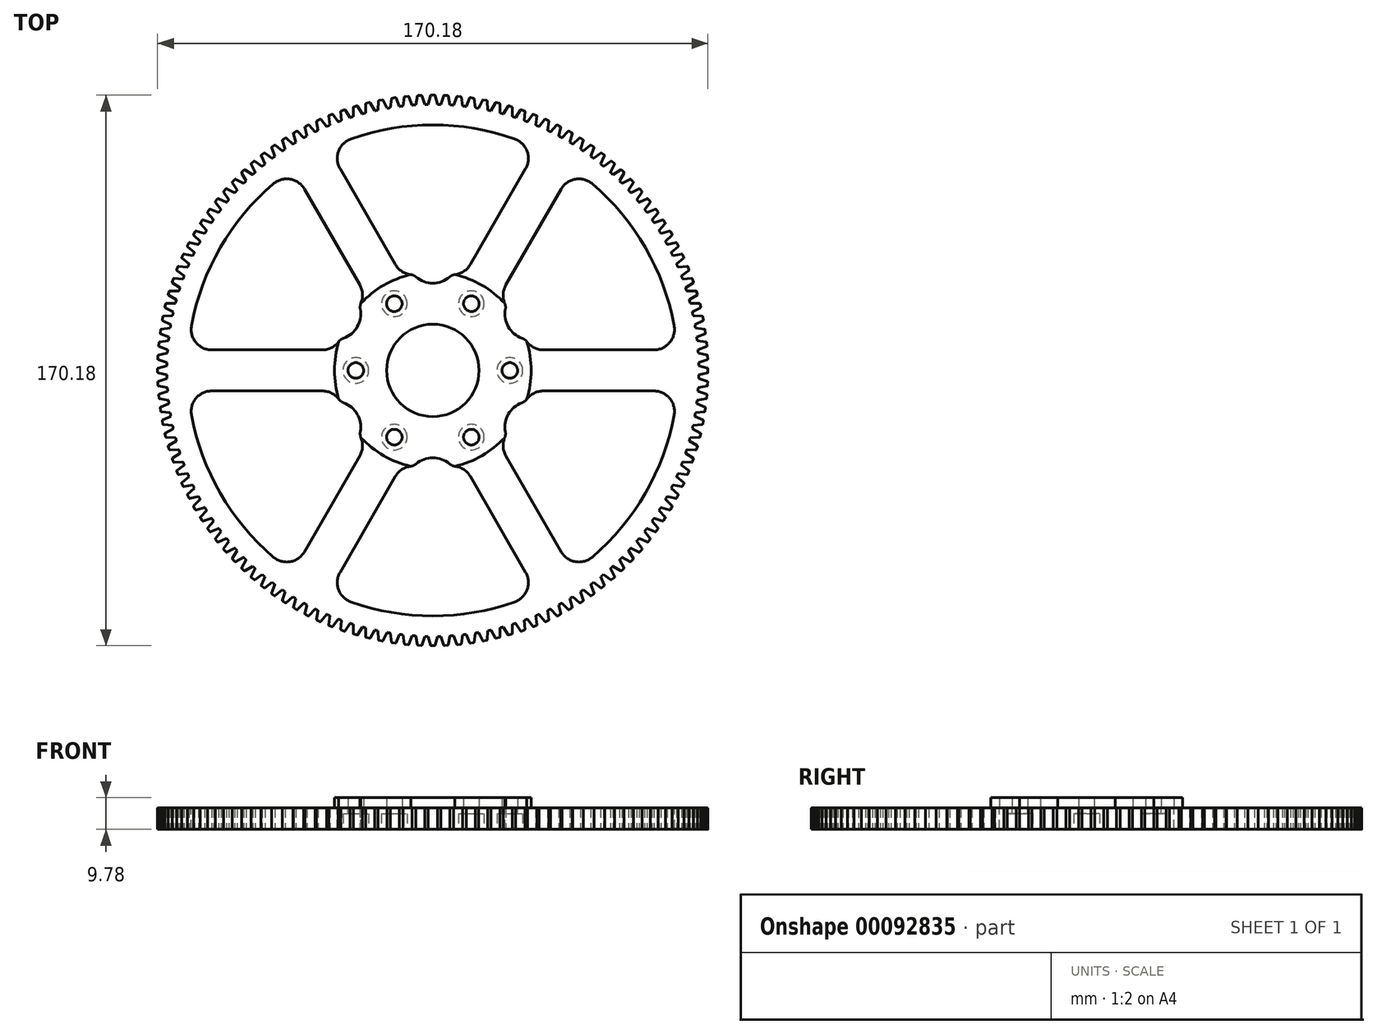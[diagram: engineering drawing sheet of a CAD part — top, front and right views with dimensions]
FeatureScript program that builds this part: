
annotation { "Feature Type Name" : "Feature", "Feature Type Description" : "" }
export const myFeature = defineFeature(function(context is Context, id is Id, definition is map)
    precondition{}
    {
        {
            var Q0;
            Q0=qCreatedBy(makeId("Top.planeOp"),FACE);
            var sketch = newSketch(context, id + "F0", { "sketchPlane" : qUnion([Q0])});
            skArc(sketch, "E0", {"start": v(-1.4, 82.23) * mm, "mid": v(-82.23, -1.4) * mm, "end": v(1.4, -82.23) * mm});
            skArc(sketch, "E1", {"start": v(1.4, -82.23) * mm, "mid": v(82.24, 0) * mm, "end": v(1.4, 82.23) * mm});
            skLineSegment(sketch, "E2", {"start": v(1.4, 82.23) * mm, "end": v(0.7, 84.97) * mm});
            skArc(sketch, "E3", {"start": v(0.7, 84.97) * mm, "mid": v(0.64, 85.06) * mm, "end": v(0.55, 85.1) * mm});
            skLineSegment(sketch, "E4", {"start": v(-1.4, 82.23) * mm, "end": v(-0.7, 84.97) * mm});
            skArc(sketch, "E5", {"start": v(-0.55, 85.1) * mm, "mid": v(-0.64, 85.06) * mm, "end": v(-0.7, 84.97) * mm});
            skLineSegment(sketch, "E6", {"start": v(-0.55, 85.1) * mm, "end": v(0.55, 85.1) * mm});
            skArc(sketch, "E7", {"start": v(1.4, 82.23) * mm, "mid": v(0, 82.24) * mm, "end": v(-1.4, 82.23) * mm});
            skSolve(sketch);
        }
        {
            var Q0;
            Q0=makeQuery(id+"F0.imprint","IMPRINT",FACE,{"disambiguationData":[TD([[makeQuery(id+"F0.imprint","IMPRINT",EDGE,{"derivedFrom":sQuery(id+"F0.wireOp",EDGE,"E0")}),1.0]])]});
            extrude(context, id + "F1", {"entities" : qUnion([Q0]), "depth" : 6.6 * mm, "symmetric" : true});
        }
        {
            var Q0;
            Q0=makeQuery(id+"F0.imprint","IMPRINT",FACE,{"disambiguationData":[TD([[makeQuery(id+"F0.imprint","IMPRINT",EDGE,{"derivedFrom":sQuery(id+"F0.wireOp",EDGE,"E2")}),1.0]])]});
            var Q1;
            Q1=makeQuery(id+"F1.opExtrude","CAP_FACE",FACE,{"disambiguationData":[OSD([sQuery(id+"F0.wireOp",EDGE,"E0"),sQuery(id+"F0.wireOp",EDGE,"E1"),sQuery(id+"F0.wireOp",EDGE,"E7")])],"isStart":false});
            var Q2;
            Q2=makeQuery(id+"F1.opExtrude","CAP_FACE",FACE,{"disambiguationData":[OSD([sQuery(id+"F0.wireOp",EDGE,"E0"),sQuery(id+"F0.wireOp",EDGE,"E1"),sQuery(id+"F0.wireOp",EDGE,"E7")])],"isStart":true});
            extrude(context, id + "F2", {"entities" : qUnion([Q0]), "endBound" : BoundingType.UP_TO_SURFACE, "endBoundEntityFace" : qUnion([Q1]), "depth" : 25.4 * mm, "hasSecondDirection" : true, "secondDirectionBound" : BoundingType.UP_TO_SURFACE, "secondDirectionOppositeDirection" : true, "secondDirectionBoundEntityFace" : qUnion([Q2]), "secondDirectionDepth" : 25.4 * mm});
        }
        {
            var Q0;
            Q0=makeQuery(id+"F2.opExtrude","SWEPT_BODY",BODY,{"disambiguationData":[OSD([sQuery(id+"F0.wireOp",EDGE,"E2"),sQuery(id+"F0.wireOp",EDGE,"E3"),sQuery(id+"F0.wireOp",EDGE,"E4"),sQuery(id+"F0.wireOp",EDGE,"E5"),sQuery(id+"F0.wireOp",EDGE,"E6"),sQuery(id+"F0.wireOp",EDGE,"E7")])]});
            var Q1;
            Q1=makeQuery(id+"F1.opExtrude","CAP_EDGE",EDGE,{"disambiguationData":[OSD([sQuery(id+"F0.wireOp",EDGE,"E0"),sQuery(id+"F0.wireOp",EDGE,"E1"),sQuery(id+"F0.wireOp",EDGE,"E7")])],"isStart":false});
            circularPattern(context, id + "F3", {"operationType" : NewBodyOperationType.ADD, "entities" : qUnion([Q0]), "axis" : qUnion([Q1]), "angle" : 360 * degree, "instanceCount" : 132, "oppositeDirection" : true, "equalSpace" : true});
        }
        {
            var Q0;
            {var subQ0=sQuery(id+"F0.wireOp",EDGE,"E7");var subQ1=makeQuery(id+"F2.opExtrude","CAP_FACE",FACE,{"disambiguationData":[OSD([sQuery(id+"F0.wireOp",EDGE,"E2"),sQuery(id+"F0.wireOp",EDGE,"E3"),sQuery(id+"F0.wireOp",EDGE,"E4"),sQuery(id+"F0.wireOp",EDGE,"E5"),sQuery(id+"F0.wireOp",EDGE,"E6"),subQ0])],"isStart":false});Q0=makeQuery(id+"F3.boolean.opBoolean","MERGE",FACE,{"derivedFrom":[makeQuery(id+"F1.opExtrude","CAP_FACE",FACE,{"disambiguationData":[OSD([sQuery(id+"F0.wireOp",EDGE,"E0"),sQuery(id+"F0.wireOp",EDGE,"E1"),subQ0])],"isStart":false}),subQ1,makeQuery(id+"F3.opPattern","COPY",FACE,{"derivedFrom":subQ1,"instanceName":"1"}),makeQuery(id+"F3.opPattern","COPY",FACE,{"derivedFrom":subQ1,"instanceName":"2"}),makeQuery(id+"F3.opPattern","COPY",FACE,{"derivedFrom":subQ1,"instanceName":"3"}),makeQuery(id+"F3.opPattern","COPY",FACE,{"derivedFrom":subQ1,"instanceName":"4"}),makeQuery(id+"F3.opPattern","COPY",FACE,{"derivedFrom":subQ1,"instanceName":"5"}),makeQuery(id+"F3.opPattern","COPY",FACE,{"derivedFrom":subQ1,"instanceName":"6"}),makeQuery(id+"F3.opPattern","COPY",FACE,{"derivedFrom":subQ1,"instanceName":"7"}),makeQuery(id+"F3.opPattern","COPY",FACE,{"derivedFrom":subQ1,"instanceName":"8"}),makeQuery(id+"F3.opPattern","COPY",FACE,{"derivedFrom":subQ1,"instanceName":"9"}),makeQuery(id+"F3.opPattern","COPY",FACE,{"derivedFrom":subQ1,"instanceName":"10"}),makeQuery(id+"F3.opPattern","COPY",FACE,{"derivedFrom":subQ1,"instanceName":"11"}),makeQuery(id+"F3.opPattern","COPY",FACE,{"derivedFrom":subQ1,"instanceName":"12"}),makeQuery(id+"F3.opPattern","COPY",FACE,{"derivedFrom":subQ1,"instanceName":"13"}),makeQuery(id+"F3.opPattern","COPY",FACE,{"derivedFrom":subQ1,"instanceName":"14"}),makeQuery(id+"F3.opPattern","COPY",FACE,{"derivedFrom":subQ1,"instanceName":"15"}),makeQuery(id+"F3.opPattern","COPY",FACE,{"derivedFrom":subQ1,"instanceName":"16"}),makeQuery(id+"F3.opPattern","COPY",FACE,{"derivedFrom":subQ1,"instanceName":"17"}),makeQuery(id+"F3.opPattern","COPY",FACE,{"derivedFrom":subQ1,"instanceName":"18"}),makeQuery(id+"F3.opPattern","COPY",FACE,{"derivedFrom":subQ1,"instanceName":"19"}),makeQuery(id+"F3.opPattern","COPY",FACE,{"derivedFrom":subQ1,"instanceName":"20"}),makeQuery(id+"F3.opPattern","COPY",FACE,{"derivedFrom":subQ1,"instanceName":"21"}),makeQuery(id+"F3.opPattern","COPY",FACE,{"derivedFrom":subQ1,"instanceName":"22"}),makeQuery(id+"F3.opPattern","COPY",FACE,{"derivedFrom":subQ1,"instanceName":"23"}),makeQuery(id+"F3.opPattern","COPY",FACE,{"derivedFrom":subQ1,"instanceName":"24"}),makeQuery(id+"F3.opPattern","COPY",FACE,{"derivedFrom":subQ1,"instanceName":"25"}),makeQuery(id+"F3.opPattern","COPY",FACE,{"derivedFrom":subQ1,"instanceName":"26"}),makeQuery(id+"F3.opPattern","COPY",FACE,{"derivedFrom":subQ1,"instanceName":"27"}),makeQuery(id+"F3.opPattern","COPY",FACE,{"derivedFrom":subQ1,"instanceName":"28"}),makeQuery(id+"F3.opPattern","COPY",FACE,{"derivedFrom":subQ1,"instanceName":"29"}),makeQuery(id+"F3.opPattern","COPY",FACE,{"derivedFrom":subQ1,"instanceName":"30"}),makeQuery(id+"F3.opPattern","COPY",FACE,{"derivedFrom":subQ1,"instanceName":"31"}),makeQuery(id+"F3.opPattern","COPY",FACE,{"derivedFrom":subQ1,"instanceName":"32"}),makeQuery(id+"F3.opPattern","COPY",FACE,{"derivedFrom":subQ1,"instanceName":"33"}),makeQuery(id+"F3.opPattern","COPY",FACE,{"derivedFrom":subQ1,"instanceName":"34"}),makeQuery(id+"F3.opPattern","COPY",FACE,{"derivedFrom":subQ1,"instanceName":"35"}),makeQuery(id+"F3.opPattern","COPY",FACE,{"derivedFrom":subQ1,"instanceName":"36"}),makeQuery(id+"F3.opPattern","COPY",FACE,{"derivedFrom":subQ1,"instanceName":"37"}),makeQuery(id+"F3.opPattern","COPY",FACE,{"derivedFrom":subQ1,"instanceName":"38"}),makeQuery(id+"F3.opPattern","COPY",FACE,{"derivedFrom":subQ1,"instanceName":"39"}),makeQuery(id+"F3.opPattern","COPY",FACE,{"derivedFrom":subQ1,"instanceName":"40"}),makeQuery(id+"F3.opPattern","COPY",FACE,{"derivedFrom":subQ1,"instanceName":"41"}),makeQuery(id+"F3.opPattern","COPY",FACE,{"derivedFrom":subQ1,"instanceName":"42"}),makeQuery(id+"F3.opPattern","COPY",FACE,{"derivedFrom":subQ1,"instanceName":"43"}),makeQuery(id+"F3.opPattern","COPY",FACE,{"derivedFrom":subQ1,"instanceName":"44"}),makeQuery(id+"F3.opPattern","COPY",FACE,{"derivedFrom":subQ1,"instanceName":"45"}),makeQuery(id+"F3.opPattern","COPY",FACE,{"derivedFrom":subQ1,"instanceName":"46"}),makeQuery(id+"F3.opPattern","COPY",FACE,{"derivedFrom":subQ1,"instanceName":"47"}),makeQuery(id+"F3.opPattern","COPY",FACE,{"derivedFrom":subQ1,"instanceName":"48"}),makeQuery(id+"F3.opPattern","COPY",FACE,{"derivedFrom":subQ1,"instanceName":"49"}),makeQuery(id+"F3.opPattern","COPY",FACE,{"derivedFrom":subQ1,"instanceName":"50"}),makeQuery(id+"F3.opPattern","COPY",FACE,{"derivedFrom":subQ1,"instanceName":"51"}),makeQuery(id+"F3.opPattern","COPY",FACE,{"derivedFrom":subQ1,"instanceName":"52"}),makeQuery(id+"F3.opPattern","COPY",FACE,{"derivedFrom":subQ1,"instanceName":"53"}),makeQuery(id+"F3.opPattern","COPY",FACE,{"derivedFrom":subQ1,"instanceName":"54"}),makeQuery(id+"F3.opPattern","COPY",FACE,{"derivedFrom":subQ1,"instanceName":"55"}),makeQuery(id+"F3.opPattern","COPY",FACE,{"derivedFrom":subQ1,"instanceName":"56"}),makeQuery(id+"F3.opPattern","COPY",FACE,{"derivedFrom":subQ1,"instanceName":"57"}),makeQuery(id+"F3.opPattern","COPY",FACE,{"derivedFrom":subQ1,"instanceName":"58"}),makeQuery(id+"F3.opPattern","COPY",FACE,{"derivedFrom":subQ1,"instanceName":"59"}),makeQuery(id+"F3.opPattern","COPY",FACE,{"derivedFrom":subQ1,"instanceName":"60"}),makeQuery(id+"F3.opPattern","COPY",FACE,{"derivedFrom":subQ1,"instanceName":"61"}),makeQuery(id+"F3.opPattern","COPY",FACE,{"derivedFrom":subQ1,"instanceName":"62"}),makeQuery(id+"F3.opPattern","COPY",FACE,{"derivedFrom":subQ1,"instanceName":"63"}),makeQuery(id+"F3.opPattern","COPY",FACE,{"derivedFrom":subQ1,"instanceName":"64"}),makeQuery(id+"F3.opPattern","COPY",FACE,{"derivedFrom":subQ1,"instanceName":"65"}),makeQuery(id+"F3.opPattern","COPY",FACE,{"derivedFrom":subQ1,"instanceName":"66"}),makeQuery(id+"F3.opPattern","COPY",FACE,{"derivedFrom":subQ1,"instanceName":"67"}),makeQuery(id+"F3.opPattern","COPY",FACE,{"derivedFrom":subQ1,"instanceName":"68"}),makeQuery(id+"F3.opPattern","COPY",FACE,{"derivedFrom":subQ1,"instanceName":"69"}),makeQuery(id+"F3.opPattern","COPY",FACE,{"derivedFrom":subQ1,"instanceName":"70"}),makeQuery(id+"F3.opPattern","COPY",FACE,{"derivedFrom":subQ1,"instanceName":"71"}),makeQuery(id+"F3.opPattern","COPY",FACE,{"derivedFrom":subQ1,"instanceName":"72"}),makeQuery(id+"F3.opPattern","COPY",FACE,{"derivedFrom":subQ1,"instanceName":"73"}),makeQuery(id+"F3.opPattern","COPY",FACE,{"derivedFrom":subQ1,"instanceName":"74"}),makeQuery(id+"F3.opPattern","COPY",FACE,{"derivedFrom":subQ1,"instanceName":"75"}),makeQuery(id+"F3.opPattern","COPY",FACE,{"derivedFrom":subQ1,"instanceName":"76"}),makeQuery(id+"F3.opPattern","COPY",FACE,{"derivedFrom":subQ1,"instanceName":"77"}),makeQuery(id+"F3.opPattern","COPY",FACE,{"derivedFrom":subQ1,"instanceName":"78"}),makeQuery(id+"F3.opPattern","COPY",FACE,{"derivedFrom":subQ1,"instanceName":"79"}),makeQuery(id+"F3.opPattern","COPY",FACE,{"derivedFrom":subQ1,"instanceName":"80"}),makeQuery(id+"F3.opPattern","COPY",FACE,{"derivedFrom":subQ1,"instanceName":"81"}),makeQuery(id+"F3.opPattern","COPY",FACE,{"derivedFrom":subQ1,"instanceName":"82"}),makeQuery(id+"F3.opPattern","COPY",FACE,{"derivedFrom":subQ1,"instanceName":"83"}),makeQuery(id+"F3.opPattern","COPY",FACE,{"derivedFrom":subQ1,"instanceName":"84"}),makeQuery(id+"F3.opPattern","COPY",FACE,{"derivedFrom":subQ1,"instanceName":"85"}),makeQuery(id+"F3.opPattern","COPY",FACE,{"derivedFrom":subQ1,"instanceName":"86"}),makeQuery(id+"F3.opPattern","COPY",FACE,{"derivedFrom":subQ1,"instanceName":"87"}),makeQuery(id+"F3.opPattern","COPY",FACE,{"derivedFrom":subQ1,"instanceName":"88"}),makeQuery(id+"F3.opPattern","COPY",FACE,{"derivedFrom":subQ1,"instanceName":"89"}),makeQuery(id+"F3.opPattern","COPY",FACE,{"derivedFrom":subQ1,"instanceName":"90"}),makeQuery(id+"F3.opPattern","COPY",FACE,{"derivedFrom":subQ1,"instanceName":"91"}),makeQuery(id+"F3.opPattern","COPY",FACE,{"derivedFrom":subQ1,"instanceName":"92"}),makeQuery(id+"F3.opPattern","COPY",FACE,{"derivedFrom":subQ1,"instanceName":"93"}),makeQuery(id+"F3.opPattern","COPY",FACE,{"derivedFrom":subQ1,"instanceName":"94"}),makeQuery(id+"F3.opPattern","COPY",FACE,{"derivedFrom":subQ1,"instanceName":"95"}),makeQuery(id+"F3.opPattern","COPY",FACE,{"derivedFrom":subQ1,"instanceName":"96"}),makeQuery(id+"F3.opPattern","COPY",FACE,{"derivedFrom":subQ1,"instanceName":"97"}),makeQuery(id+"F3.opPattern","COPY",FACE,{"derivedFrom":subQ1,"instanceName":"98"}),makeQuery(id+"F3.opPattern","COPY",FACE,{"derivedFrom":subQ1,"instanceName":"99"}),makeQuery(id+"F3.opPattern","COPY",FACE,{"derivedFrom":subQ1,"instanceName":"100"}),makeQuery(id+"F3.opPattern","COPY",FACE,{"derivedFrom":subQ1,"instanceName":"101"}),makeQuery(id+"F3.opPattern","COPY",FACE,{"derivedFrom":subQ1,"instanceName":"102"}),makeQuery(id+"F3.opPattern","COPY",FACE,{"derivedFrom":subQ1,"instanceName":"103"}),makeQuery(id+"F3.opPattern","COPY",FACE,{"derivedFrom":subQ1,"instanceName":"104"}),makeQuery(id+"F3.opPattern","COPY",FACE,{"derivedFrom":subQ1,"instanceName":"105"}),makeQuery(id+"F3.opPattern","COPY",FACE,{"derivedFrom":subQ1,"instanceName":"106"}),makeQuery(id+"F3.opPattern","COPY",FACE,{"derivedFrom":subQ1,"instanceName":"107"}),makeQuery(id+"F3.opPattern","COPY",FACE,{"derivedFrom":subQ1,"instanceName":"108"}),makeQuery(id+"F3.opPattern","COPY",FACE,{"derivedFrom":subQ1,"instanceName":"109"}),makeQuery(id+"F3.opPattern","COPY",FACE,{"derivedFrom":subQ1,"instanceName":"110"}),makeQuery(id+"F3.opPattern","COPY",FACE,{"derivedFrom":subQ1,"instanceName":"111"}),makeQuery(id+"F3.opPattern","COPY",FACE,{"derivedFrom":subQ1,"instanceName":"112"}),makeQuery(id+"F3.opPattern","COPY",FACE,{"derivedFrom":subQ1,"instanceName":"113"}),makeQuery(id+"F3.opPattern","COPY",FACE,{"derivedFrom":subQ1,"instanceName":"114"}),makeQuery(id+"F3.opPattern","COPY",FACE,{"derivedFrom":subQ1,"instanceName":"115"}),makeQuery(id+"F3.opPattern","COPY",FACE,{"derivedFrom":subQ1,"instanceName":"116"}),makeQuery(id+"F3.opPattern","COPY",FACE,{"derivedFrom":subQ1,"instanceName":"117"}),makeQuery(id+"F3.opPattern","COPY",FACE,{"derivedFrom":subQ1,"instanceName":"118"}),makeQuery(id+"F3.opPattern","COPY",FACE,{"derivedFrom":subQ1,"instanceName":"119"}),makeQuery(id+"F3.opPattern","COPY",FACE,{"derivedFrom":subQ1,"instanceName":"120"}),makeQuery(id+"F3.opPattern","COPY",FACE,{"derivedFrom":subQ1,"instanceName":"121"}),makeQuery(id+"F3.opPattern","COPY",FACE,{"derivedFrom":subQ1,"instanceName":"122"}),makeQuery(id+"F3.opPattern","COPY",FACE,{"derivedFrom":subQ1,"instanceName":"123"}),makeQuery(id+"F3.opPattern","COPY",FACE,{"derivedFrom":subQ1,"instanceName":"124"}),makeQuery(id+"F3.opPattern","COPY",FACE,{"derivedFrom":subQ1,"instanceName":"125"}),makeQuery(id+"F3.opPattern","COPY",FACE,{"derivedFrom":subQ1,"instanceName":"126"}),makeQuery(id+"F3.opPattern","COPY",FACE,{"derivedFrom":subQ1,"instanceName":"127"}),makeQuery(id+"F3.opPattern","COPY",FACE,{"derivedFrom":subQ1,"instanceName":"128"}),makeQuery(id+"F3.opPattern","COPY",FACE,{"derivedFrom":subQ1,"instanceName":"129"}),makeQuery(id+"F3.opPattern","COPY",FACE,{"derivedFrom":subQ1,"instanceName":"130"}),makeQuery(id+"F3.opPattern","COPY",FACE,{"derivedFrom":subQ1,"instanceName":"131"})]});}
            var sketch = newSketch(context, id + "F4", { "sketchPlane" : qUnion([Q0])});
            skCircle(sketch, "E8", {"center": v(0, 0) * mm, "radius": 14.29 * mm});
            skCircle(sketch, "E9.cCircle", {"center": v(0, 0) * mm, "radius": 23.81 * mm, "construction": true});
            skLineSegment(sketch, "E9.0", {"start": v(23.81, 0) * mm, "end": v(11.9, -20.62) * mm, "construction": true});
            skLineSegment(sketch, "E9.1", {"start": v(11.9, -20.62) * mm, "end": v(-11.9, -20.62) * mm, "construction": true});
            skLineSegment(sketch, "E9.2", {"start": v(-11.9, -20.62) * mm, "end": v(-23.81, 0) * mm, "construction": true});
            skLineSegment(sketch, "E9.3", {"start": v(-23.81, 0) * mm, "end": v(-11.9, 20.62) * mm, "construction": true});
            skLineSegment(sketch, "E9.4", {"start": v(-11.9, 20.62) * mm, "end": v(11.9, 20.62) * mm, "construction": true});
            skLineSegment(sketch, "E9.5", {"start": v(11.9, 20.62) * mm, "end": v(23.81, 0) * mm, "construction": true});
            skCircle(sketch, "E10", {"center": v(-11.9, 20.62) * mm, "radius": 2.41 * mm});
            skCircle(sketch, "E11", {"center": v(-23.81, 0) * mm, "radius": 2.41 * mm});
            skCircle(sketch, "E12", {"center": v(-11.9, -20.62) * mm, "radius": 2.41 * mm});
            skCircle(sketch, "E13", {"center": v(11.9, -20.62) * mm, "radius": 2.41 * mm});
            skCircle(sketch, "E14", {"center": v(23.81, 0) * mm, "radius": 2.41 * mm});
            skCircle(sketch, "E15", {"center": v(11.9, 20.62) * mm, "radius": 2.41 * mm});
            skSolve(sketch);
        }
        {
            var Q0;
            Q0=qSketchRegion(id+"F4",true);
            extrude(context, id + "F5", {"entities" : qUnion([Q0]), "operationType" : NewBodyOperationType.REMOVE, "endBound" : BoundingType.THROUGH_ALL, "oppositeDirection" : true, "depth" : 25.4 * mm});
        }
        {
            var Q0;
            {var subQ0=sQuery(id+"F0.wireOp",EDGE,"E7");var subQ1=makeQuery(id+"F2.opExtrude","CAP_FACE",FACE,{"disambiguationData":[OSD([sQuery(id+"F0.wireOp",EDGE,"E2"),sQuery(id+"F0.wireOp",EDGE,"E3"),sQuery(id+"F0.wireOp",EDGE,"E4"),sQuery(id+"F0.wireOp",EDGE,"E5"),sQuery(id+"F0.wireOp",EDGE,"E6"),subQ0])],"isStart":false});Q0=makeQuery(id+"F3.boolean.opBoolean","MERGE",FACE,{"derivedFrom":[makeQuery(id+"F1.opExtrude","CAP_FACE",FACE,{"disambiguationData":[OSD([sQuery(id+"F0.wireOp",EDGE,"E0"),sQuery(id+"F0.wireOp",EDGE,"E1"),subQ0])],"isStart":false}),subQ1,makeQuery(id+"F3.opPattern","COPY",FACE,{"derivedFrom":subQ1,"instanceName":"1"}),makeQuery(id+"F3.opPattern","COPY",FACE,{"derivedFrom":subQ1,"instanceName":"2"}),makeQuery(id+"F3.opPattern","COPY",FACE,{"derivedFrom":subQ1,"instanceName":"3"}),makeQuery(id+"F3.opPattern","COPY",FACE,{"derivedFrom":subQ1,"instanceName":"4"}),makeQuery(id+"F3.opPattern","COPY",FACE,{"derivedFrom":subQ1,"instanceName":"5"}),makeQuery(id+"F3.opPattern","COPY",FACE,{"derivedFrom":subQ1,"instanceName":"6"}),makeQuery(id+"F3.opPattern","COPY",FACE,{"derivedFrom":subQ1,"instanceName":"7"}),makeQuery(id+"F3.opPattern","COPY",FACE,{"derivedFrom":subQ1,"instanceName":"8"}),makeQuery(id+"F3.opPattern","COPY",FACE,{"derivedFrom":subQ1,"instanceName":"9"}),makeQuery(id+"F3.opPattern","COPY",FACE,{"derivedFrom":subQ1,"instanceName":"10"}),makeQuery(id+"F3.opPattern","COPY",FACE,{"derivedFrom":subQ1,"instanceName":"11"}),makeQuery(id+"F3.opPattern","COPY",FACE,{"derivedFrom":subQ1,"instanceName":"12"}),makeQuery(id+"F3.opPattern","COPY",FACE,{"derivedFrom":subQ1,"instanceName":"13"}),makeQuery(id+"F3.opPattern","COPY",FACE,{"derivedFrom":subQ1,"instanceName":"14"}),makeQuery(id+"F3.opPattern","COPY",FACE,{"derivedFrom":subQ1,"instanceName":"15"}),makeQuery(id+"F3.opPattern","COPY",FACE,{"derivedFrom":subQ1,"instanceName":"16"}),makeQuery(id+"F3.opPattern","COPY",FACE,{"derivedFrom":subQ1,"instanceName":"17"}),makeQuery(id+"F3.opPattern","COPY",FACE,{"derivedFrom":subQ1,"instanceName":"18"}),makeQuery(id+"F3.opPattern","COPY",FACE,{"derivedFrom":subQ1,"instanceName":"19"}),makeQuery(id+"F3.opPattern","COPY",FACE,{"derivedFrom":subQ1,"instanceName":"20"}),makeQuery(id+"F3.opPattern","COPY",FACE,{"derivedFrom":subQ1,"instanceName":"21"}),makeQuery(id+"F3.opPattern","COPY",FACE,{"derivedFrom":subQ1,"instanceName":"22"}),makeQuery(id+"F3.opPattern","COPY",FACE,{"derivedFrom":subQ1,"instanceName":"23"}),makeQuery(id+"F3.opPattern","COPY",FACE,{"derivedFrom":subQ1,"instanceName":"24"}),makeQuery(id+"F3.opPattern","COPY",FACE,{"derivedFrom":subQ1,"instanceName":"25"}),makeQuery(id+"F3.opPattern","COPY",FACE,{"derivedFrom":subQ1,"instanceName":"26"}),makeQuery(id+"F3.opPattern","COPY",FACE,{"derivedFrom":subQ1,"instanceName":"27"}),makeQuery(id+"F3.opPattern","COPY",FACE,{"derivedFrom":subQ1,"instanceName":"28"}),makeQuery(id+"F3.opPattern","COPY",FACE,{"derivedFrom":subQ1,"instanceName":"29"}),makeQuery(id+"F3.opPattern","COPY",FACE,{"derivedFrom":subQ1,"instanceName":"30"}),makeQuery(id+"F3.opPattern","COPY",FACE,{"derivedFrom":subQ1,"instanceName":"31"}),makeQuery(id+"F3.opPattern","COPY",FACE,{"derivedFrom":subQ1,"instanceName":"32"}),makeQuery(id+"F3.opPattern","COPY",FACE,{"derivedFrom":subQ1,"instanceName":"33"}),makeQuery(id+"F3.opPattern","COPY",FACE,{"derivedFrom":subQ1,"instanceName":"34"}),makeQuery(id+"F3.opPattern","COPY",FACE,{"derivedFrom":subQ1,"instanceName":"35"}),makeQuery(id+"F3.opPattern","COPY",FACE,{"derivedFrom":subQ1,"instanceName":"36"}),makeQuery(id+"F3.opPattern","COPY",FACE,{"derivedFrom":subQ1,"instanceName":"37"}),makeQuery(id+"F3.opPattern","COPY",FACE,{"derivedFrom":subQ1,"instanceName":"38"}),makeQuery(id+"F3.opPattern","COPY",FACE,{"derivedFrom":subQ1,"instanceName":"39"}),makeQuery(id+"F3.opPattern","COPY",FACE,{"derivedFrom":subQ1,"instanceName":"40"}),makeQuery(id+"F3.opPattern","COPY",FACE,{"derivedFrom":subQ1,"instanceName":"41"}),makeQuery(id+"F3.opPattern","COPY",FACE,{"derivedFrom":subQ1,"instanceName":"42"}),makeQuery(id+"F3.opPattern","COPY",FACE,{"derivedFrom":subQ1,"instanceName":"43"}),makeQuery(id+"F3.opPattern","COPY",FACE,{"derivedFrom":subQ1,"instanceName":"44"}),makeQuery(id+"F3.opPattern","COPY",FACE,{"derivedFrom":subQ1,"instanceName":"45"}),makeQuery(id+"F3.opPattern","COPY",FACE,{"derivedFrom":subQ1,"instanceName":"46"}),makeQuery(id+"F3.opPattern","COPY",FACE,{"derivedFrom":subQ1,"instanceName":"47"}),makeQuery(id+"F3.opPattern","COPY",FACE,{"derivedFrom":subQ1,"instanceName":"48"}),makeQuery(id+"F3.opPattern","COPY",FACE,{"derivedFrom":subQ1,"instanceName":"49"}),makeQuery(id+"F3.opPattern","COPY",FACE,{"derivedFrom":subQ1,"instanceName":"50"}),makeQuery(id+"F3.opPattern","COPY",FACE,{"derivedFrom":subQ1,"instanceName":"51"}),makeQuery(id+"F3.opPattern","COPY",FACE,{"derivedFrom":subQ1,"instanceName":"52"}),makeQuery(id+"F3.opPattern","COPY",FACE,{"derivedFrom":subQ1,"instanceName":"53"}),makeQuery(id+"F3.opPattern","COPY",FACE,{"derivedFrom":subQ1,"instanceName":"54"}),makeQuery(id+"F3.opPattern","COPY",FACE,{"derivedFrom":subQ1,"instanceName":"55"}),makeQuery(id+"F3.opPattern","COPY",FACE,{"derivedFrom":subQ1,"instanceName":"56"}),makeQuery(id+"F3.opPattern","COPY",FACE,{"derivedFrom":subQ1,"instanceName":"57"}),makeQuery(id+"F3.opPattern","COPY",FACE,{"derivedFrom":subQ1,"instanceName":"58"}),makeQuery(id+"F3.opPattern","COPY",FACE,{"derivedFrom":subQ1,"instanceName":"59"}),makeQuery(id+"F3.opPattern","COPY",FACE,{"derivedFrom":subQ1,"instanceName":"60"}),makeQuery(id+"F3.opPattern","COPY",FACE,{"derivedFrom":subQ1,"instanceName":"61"}),makeQuery(id+"F3.opPattern","COPY",FACE,{"derivedFrom":subQ1,"instanceName":"62"}),makeQuery(id+"F3.opPattern","COPY",FACE,{"derivedFrom":subQ1,"instanceName":"63"}),makeQuery(id+"F3.opPattern","COPY",FACE,{"derivedFrom":subQ1,"instanceName":"64"}),makeQuery(id+"F3.opPattern","COPY",FACE,{"derivedFrom":subQ1,"instanceName":"65"}),makeQuery(id+"F3.opPattern","COPY",FACE,{"derivedFrom":subQ1,"instanceName":"66"}),makeQuery(id+"F3.opPattern","COPY",FACE,{"derivedFrom":subQ1,"instanceName":"67"}),makeQuery(id+"F3.opPattern","COPY",FACE,{"derivedFrom":subQ1,"instanceName":"68"}),makeQuery(id+"F3.opPattern","COPY",FACE,{"derivedFrom":subQ1,"instanceName":"69"}),makeQuery(id+"F3.opPattern","COPY",FACE,{"derivedFrom":subQ1,"instanceName":"70"}),makeQuery(id+"F3.opPattern","COPY",FACE,{"derivedFrom":subQ1,"instanceName":"71"}),makeQuery(id+"F3.opPattern","COPY",FACE,{"derivedFrom":subQ1,"instanceName":"72"}),makeQuery(id+"F3.opPattern","COPY",FACE,{"derivedFrom":subQ1,"instanceName":"73"}),makeQuery(id+"F3.opPattern","COPY",FACE,{"derivedFrom":subQ1,"instanceName":"74"}),makeQuery(id+"F3.opPattern","COPY",FACE,{"derivedFrom":subQ1,"instanceName":"75"}),makeQuery(id+"F3.opPattern","COPY",FACE,{"derivedFrom":subQ1,"instanceName":"76"}),makeQuery(id+"F3.opPattern","COPY",FACE,{"derivedFrom":subQ1,"instanceName":"77"}),makeQuery(id+"F3.opPattern","COPY",FACE,{"derivedFrom":subQ1,"instanceName":"78"}),makeQuery(id+"F3.opPattern","COPY",FACE,{"derivedFrom":subQ1,"instanceName":"79"}),makeQuery(id+"F3.opPattern","COPY",FACE,{"derivedFrom":subQ1,"instanceName":"80"}),makeQuery(id+"F3.opPattern","COPY",FACE,{"derivedFrom":subQ1,"instanceName":"81"}),makeQuery(id+"F3.opPattern","COPY",FACE,{"derivedFrom":subQ1,"instanceName":"82"}),makeQuery(id+"F3.opPattern","COPY",FACE,{"derivedFrom":subQ1,"instanceName":"83"}),makeQuery(id+"F3.opPattern","COPY",FACE,{"derivedFrom":subQ1,"instanceName":"84"}),makeQuery(id+"F3.opPattern","COPY",FACE,{"derivedFrom":subQ1,"instanceName":"85"}),makeQuery(id+"F3.opPattern","COPY",FACE,{"derivedFrom":subQ1,"instanceName":"86"}),makeQuery(id+"F3.opPattern","COPY",FACE,{"derivedFrom":subQ1,"instanceName":"87"}),makeQuery(id+"F3.opPattern","COPY",FACE,{"derivedFrom":subQ1,"instanceName":"88"}),makeQuery(id+"F3.opPattern","COPY",FACE,{"derivedFrom":subQ1,"instanceName":"89"}),makeQuery(id+"F3.opPattern","COPY",FACE,{"derivedFrom":subQ1,"instanceName":"90"}),makeQuery(id+"F3.opPattern","COPY",FACE,{"derivedFrom":subQ1,"instanceName":"91"}),makeQuery(id+"F3.opPattern","COPY",FACE,{"derivedFrom":subQ1,"instanceName":"92"}),makeQuery(id+"F3.opPattern","COPY",FACE,{"derivedFrom":subQ1,"instanceName":"93"}),makeQuery(id+"F3.opPattern","COPY",FACE,{"derivedFrom":subQ1,"instanceName":"94"}),makeQuery(id+"F3.opPattern","COPY",FACE,{"derivedFrom":subQ1,"instanceName":"95"}),makeQuery(id+"F3.opPattern","COPY",FACE,{"derivedFrom":subQ1,"instanceName":"96"}),makeQuery(id+"F3.opPattern","COPY",FACE,{"derivedFrom":subQ1,"instanceName":"97"}),makeQuery(id+"F3.opPattern","COPY",FACE,{"derivedFrom":subQ1,"instanceName":"98"}),makeQuery(id+"F3.opPattern","COPY",FACE,{"derivedFrom":subQ1,"instanceName":"99"}),makeQuery(id+"F3.opPattern","COPY",FACE,{"derivedFrom":subQ1,"instanceName":"100"}),makeQuery(id+"F3.opPattern","COPY",FACE,{"derivedFrom":subQ1,"instanceName":"101"}),makeQuery(id+"F3.opPattern","COPY",FACE,{"derivedFrom":subQ1,"instanceName":"102"}),makeQuery(id+"F3.opPattern","COPY",FACE,{"derivedFrom":subQ1,"instanceName":"103"}),makeQuery(id+"F3.opPattern","COPY",FACE,{"derivedFrom":subQ1,"instanceName":"104"}),makeQuery(id+"F3.opPattern","COPY",FACE,{"derivedFrom":subQ1,"instanceName":"105"}),makeQuery(id+"F3.opPattern","COPY",FACE,{"derivedFrom":subQ1,"instanceName":"106"}),makeQuery(id+"F3.opPattern","COPY",FACE,{"derivedFrom":subQ1,"instanceName":"107"}),makeQuery(id+"F3.opPattern","COPY",FACE,{"derivedFrom":subQ1,"instanceName":"108"}),makeQuery(id+"F3.opPattern","COPY",FACE,{"derivedFrom":subQ1,"instanceName":"109"}),makeQuery(id+"F3.opPattern","COPY",FACE,{"derivedFrom":subQ1,"instanceName":"110"}),makeQuery(id+"F3.opPattern","COPY",FACE,{"derivedFrom":subQ1,"instanceName":"111"}),makeQuery(id+"F3.opPattern","COPY",FACE,{"derivedFrom":subQ1,"instanceName":"112"}),makeQuery(id+"F3.opPattern","COPY",FACE,{"derivedFrom":subQ1,"instanceName":"113"}),makeQuery(id+"F3.opPattern","COPY",FACE,{"derivedFrom":subQ1,"instanceName":"114"}),makeQuery(id+"F3.opPattern","COPY",FACE,{"derivedFrom":subQ1,"instanceName":"115"}),makeQuery(id+"F3.opPattern","COPY",FACE,{"derivedFrom":subQ1,"instanceName":"116"}),makeQuery(id+"F3.opPattern","COPY",FACE,{"derivedFrom":subQ1,"instanceName":"117"}),makeQuery(id+"F3.opPattern","COPY",FACE,{"derivedFrom":subQ1,"instanceName":"118"}),makeQuery(id+"F3.opPattern","COPY",FACE,{"derivedFrom":subQ1,"instanceName":"119"}),makeQuery(id+"F3.opPattern","COPY",FACE,{"derivedFrom":subQ1,"instanceName":"120"}),makeQuery(id+"F3.opPattern","COPY",FACE,{"derivedFrom":subQ1,"instanceName":"121"}),makeQuery(id+"F3.opPattern","COPY",FACE,{"derivedFrom":subQ1,"instanceName":"122"}),makeQuery(id+"F3.opPattern","COPY",FACE,{"derivedFrom":subQ1,"instanceName":"123"}),makeQuery(id+"F3.opPattern","COPY",FACE,{"derivedFrom":subQ1,"instanceName":"124"}),makeQuery(id+"F3.opPattern","COPY",FACE,{"derivedFrom":subQ1,"instanceName":"125"}),makeQuery(id+"F3.opPattern","COPY",FACE,{"derivedFrom":subQ1,"instanceName":"126"}),makeQuery(id+"F3.opPattern","COPY",FACE,{"derivedFrom":subQ1,"instanceName":"127"}),makeQuery(id+"F3.opPattern","COPY",FACE,{"derivedFrom":subQ1,"instanceName":"128"}),makeQuery(id+"F3.opPattern","COPY",FACE,{"derivedFrom":subQ1,"instanceName":"129"}),makeQuery(id+"F3.opPattern","COPY",FACE,{"derivedFrom":subQ1,"instanceName":"130"}),makeQuery(id+"F3.opPattern","COPY",FACE,{"derivedFrom":subQ1,"instanceName":"131"})]});}
            var sketch = newSketch(context, id + "F6", { "sketchPlane" : qUnion([Q0])});
            skArc(sketch, "E16", {"start": v(-37.95, 65.73) * mm, "mid": v(-65.73, 37.95) * mm, "end": v(-75.9, 0) * mm});
            skArc(sketch, "E17", {"start": v(-15.08, 26.12) * mm, "mid": v(-26.12, 15.08) * mm, "end": v(-30.16, 0) * mm});
            skLineSegment(sketch, "E18", {"start": v(-15.08, 26.12) * mm, "end": v(-37.95, 65.73) * mm, "construction": true});
            skLineSegment(sketch, "E19", {"start": v(-30.16, 0) * mm, "end": v(-75.9, 0) * mm, "construction": true});
            skPoint(sketch, "E20", {"position": v(-23.81, 0) * mm});
            skLineSegment(sketch, "E21.0", {"start": v(-29.49, 6.35) * mm, "end": v(-75.63, 6.35) * mm});
            skLineSegment(sketch, "E22.0", {"start": v(-20.24, 22.36) * mm, "end": v(-43.31, 62.32) * mm});
            skPoint(sketch, "E23", {"position": v(-11.9, 20.62) * mm});
            skArc(sketch, "E24", {"start": v(-28.56, 9.7) * mm, "mid": v(-23.37, 13.5) * mm, "end": v(-22.69, 19.88) * mm});
            skCircle(sketch, "E25", {"center": v(0, 0) * mm, "radius": 34.93 * mm, "construction": true});
            skLineSegment(sketch, "E26", {"start": v(-26.12, 15.08) * mm, "end": v(0, 0) * mm, "construction": true});
            skSolve(sketch);
        }
        {
            var Q0;
            {var subQ0=sQuery(id+"F6.wireOp",EDGE,"E21.0");Q0=makeQuery(id+"F6.imprint","IMPRINT",FACE,{"disambiguationData":[TD([[makeQuery(id+"F6.imprint","IMPRINT",EDGE,{"derivedFrom":subQ0}),-1.0]])]});}
            var Q1;
            {var subQ0=sQuery(id+"F6.wireOp",EDGE,"E24");Q1=makeQuery(id+"F6.imprint","IMPRINT",FACE,{"disambiguationData":[TD([[makeQuery(id+"F6.imprint","IMPRINT",EDGE,{"derivedFrom":subQ0}),1.0]])]});}
            var Q2;
            {var subQ0=sQuery(id+"F0.wireOp",EDGE,"E7");var subQ1=makeQuery(id+"F2.opExtrude","CAP_FACE",FACE,{"disambiguationData":[OSD([sQuery(id+"F0.wireOp",EDGE,"E2"),sQuery(id+"F0.wireOp",EDGE,"E3"),sQuery(id+"F0.wireOp",EDGE,"E4"),sQuery(id+"F0.wireOp",EDGE,"E5"),sQuery(id+"F0.wireOp",EDGE,"E6"),subQ0])],"isStart":true});Q2=makeQuery(id+"F3.boolean.opBoolean","MERGE",FACE,{"derivedFrom":[makeQuery(id+"F1.opExtrude","CAP_FACE",FACE,{"disambiguationData":[OSD([sQuery(id+"F0.wireOp",EDGE,"E0"),sQuery(id+"F0.wireOp",EDGE,"E1"),subQ0])],"isStart":true}),subQ1,makeQuery(id+"F3.opPattern","COPY",FACE,{"derivedFrom":subQ1,"instanceName":"1"}),makeQuery(id+"F3.opPattern","COPY",FACE,{"derivedFrom":subQ1,"instanceName":"2"}),makeQuery(id+"F3.opPattern","COPY",FACE,{"derivedFrom":subQ1,"instanceName":"3"}),makeQuery(id+"F3.opPattern","COPY",FACE,{"derivedFrom":subQ1,"instanceName":"4"}),makeQuery(id+"F3.opPattern","COPY",FACE,{"derivedFrom":subQ1,"instanceName":"5"}),makeQuery(id+"F3.opPattern","COPY",FACE,{"derivedFrom":subQ1,"instanceName":"6"}),makeQuery(id+"F3.opPattern","COPY",FACE,{"derivedFrom":subQ1,"instanceName":"7"}),makeQuery(id+"F3.opPattern","COPY",FACE,{"derivedFrom":subQ1,"instanceName":"8"}),makeQuery(id+"F3.opPattern","COPY",FACE,{"derivedFrom":subQ1,"instanceName":"9"}),makeQuery(id+"F3.opPattern","COPY",FACE,{"derivedFrom":subQ1,"instanceName":"10"}),makeQuery(id+"F3.opPattern","COPY",FACE,{"derivedFrom":subQ1,"instanceName":"11"}),makeQuery(id+"F3.opPattern","COPY",FACE,{"derivedFrom":subQ1,"instanceName":"12"}),makeQuery(id+"F3.opPattern","COPY",FACE,{"derivedFrom":subQ1,"instanceName":"13"}),makeQuery(id+"F3.opPattern","COPY",FACE,{"derivedFrom":subQ1,"instanceName":"14"}),makeQuery(id+"F3.opPattern","COPY",FACE,{"derivedFrom":subQ1,"instanceName":"15"}),makeQuery(id+"F3.opPattern","COPY",FACE,{"derivedFrom":subQ1,"instanceName":"16"}),makeQuery(id+"F3.opPattern","COPY",FACE,{"derivedFrom":subQ1,"instanceName":"17"}),makeQuery(id+"F3.opPattern","COPY",FACE,{"derivedFrom":subQ1,"instanceName":"18"}),makeQuery(id+"F3.opPattern","COPY",FACE,{"derivedFrom":subQ1,"instanceName":"19"}),makeQuery(id+"F3.opPattern","COPY",FACE,{"derivedFrom":subQ1,"instanceName":"20"}),makeQuery(id+"F3.opPattern","COPY",FACE,{"derivedFrom":subQ1,"instanceName":"21"}),makeQuery(id+"F3.opPattern","COPY",FACE,{"derivedFrom":subQ1,"instanceName":"22"}),makeQuery(id+"F3.opPattern","COPY",FACE,{"derivedFrom":subQ1,"instanceName":"23"}),makeQuery(id+"F3.opPattern","COPY",FACE,{"derivedFrom":subQ1,"instanceName":"24"}),makeQuery(id+"F3.opPattern","COPY",FACE,{"derivedFrom":subQ1,"instanceName":"25"}),makeQuery(id+"F3.opPattern","COPY",FACE,{"derivedFrom":subQ1,"instanceName":"26"}),makeQuery(id+"F3.opPattern","COPY",FACE,{"derivedFrom":subQ1,"instanceName":"27"}),makeQuery(id+"F3.opPattern","COPY",FACE,{"derivedFrom":subQ1,"instanceName":"28"}),makeQuery(id+"F3.opPattern","COPY",FACE,{"derivedFrom":subQ1,"instanceName":"29"}),makeQuery(id+"F3.opPattern","COPY",FACE,{"derivedFrom":subQ1,"instanceName":"30"}),makeQuery(id+"F3.opPattern","COPY",FACE,{"derivedFrom":subQ1,"instanceName":"31"}),makeQuery(id+"F3.opPattern","COPY",FACE,{"derivedFrom":subQ1,"instanceName":"32"}),makeQuery(id+"F3.opPattern","COPY",FACE,{"derivedFrom":subQ1,"instanceName":"33"}),makeQuery(id+"F3.opPattern","COPY",FACE,{"derivedFrom":subQ1,"instanceName":"34"}),makeQuery(id+"F3.opPattern","COPY",FACE,{"derivedFrom":subQ1,"instanceName":"35"}),makeQuery(id+"F3.opPattern","COPY",FACE,{"derivedFrom":subQ1,"instanceName":"36"}),makeQuery(id+"F3.opPattern","COPY",FACE,{"derivedFrom":subQ1,"instanceName":"37"}),makeQuery(id+"F3.opPattern","COPY",FACE,{"derivedFrom":subQ1,"instanceName":"38"}),makeQuery(id+"F3.opPattern","COPY",FACE,{"derivedFrom":subQ1,"instanceName":"39"}),makeQuery(id+"F3.opPattern","COPY",FACE,{"derivedFrom":subQ1,"instanceName":"40"}),makeQuery(id+"F3.opPattern","COPY",FACE,{"derivedFrom":subQ1,"instanceName":"41"}),makeQuery(id+"F3.opPattern","COPY",FACE,{"derivedFrom":subQ1,"instanceName":"42"}),makeQuery(id+"F3.opPattern","COPY",FACE,{"derivedFrom":subQ1,"instanceName":"43"}),makeQuery(id+"F3.opPattern","COPY",FACE,{"derivedFrom":subQ1,"instanceName":"44"}),makeQuery(id+"F3.opPattern","COPY",FACE,{"derivedFrom":subQ1,"instanceName":"45"}),makeQuery(id+"F3.opPattern","COPY",FACE,{"derivedFrom":subQ1,"instanceName":"46"}),makeQuery(id+"F3.opPattern","COPY",FACE,{"derivedFrom":subQ1,"instanceName":"47"}),makeQuery(id+"F3.opPattern","COPY",FACE,{"derivedFrom":subQ1,"instanceName":"48"}),makeQuery(id+"F3.opPattern","COPY",FACE,{"derivedFrom":subQ1,"instanceName":"49"}),makeQuery(id+"F3.opPattern","COPY",FACE,{"derivedFrom":subQ1,"instanceName":"50"}),makeQuery(id+"F3.opPattern","COPY",FACE,{"derivedFrom":subQ1,"instanceName":"51"}),makeQuery(id+"F3.opPattern","COPY",FACE,{"derivedFrom":subQ1,"instanceName":"52"}),makeQuery(id+"F3.opPattern","COPY",FACE,{"derivedFrom":subQ1,"instanceName":"53"}),makeQuery(id+"F3.opPattern","COPY",FACE,{"derivedFrom":subQ1,"instanceName":"54"}),makeQuery(id+"F3.opPattern","COPY",FACE,{"derivedFrom":subQ1,"instanceName":"55"}),makeQuery(id+"F3.opPattern","COPY",FACE,{"derivedFrom":subQ1,"instanceName":"56"}),makeQuery(id+"F3.opPattern","COPY",FACE,{"derivedFrom":subQ1,"instanceName":"57"}),makeQuery(id+"F3.opPattern","COPY",FACE,{"derivedFrom":subQ1,"instanceName":"58"}),makeQuery(id+"F3.opPattern","COPY",FACE,{"derivedFrom":subQ1,"instanceName":"59"}),makeQuery(id+"F3.opPattern","COPY",FACE,{"derivedFrom":subQ1,"instanceName":"60"}),makeQuery(id+"F3.opPattern","COPY",FACE,{"derivedFrom":subQ1,"instanceName":"61"}),makeQuery(id+"F3.opPattern","COPY",FACE,{"derivedFrom":subQ1,"instanceName":"62"}),makeQuery(id+"F3.opPattern","COPY",FACE,{"derivedFrom":subQ1,"instanceName":"63"}),makeQuery(id+"F3.opPattern","COPY",FACE,{"derivedFrom":subQ1,"instanceName":"64"}),makeQuery(id+"F3.opPattern","COPY",FACE,{"derivedFrom":subQ1,"instanceName":"65"}),makeQuery(id+"F3.opPattern","COPY",FACE,{"derivedFrom":subQ1,"instanceName":"66"}),makeQuery(id+"F3.opPattern","COPY",FACE,{"derivedFrom":subQ1,"instanceName":"67"}),makeQuery(id+"F3.opPattern","COPY",FACE,{"derivedFrom":subQ1,"instanceName":"68"}),makeQuery(id+"F3.opPattern","COPY",FACE,{"derivedFrom":subQ1,"instanceName":"69"}),makeQuery(id+"F3.opPattern","COPY",FACE,{"derivedFrom":subQ1,"instanceName":"70"}),makeQuery(id+"F3.opPattern","COPY",FACE,{"derivedFrom":subQ1,"instanceName":"71"}),makeQuery(id+"F3.opPattern","COPY",FACE,{"derivedFrom":subQ1,"instanceName":"72"}),makeQuery(id+"F3.opPattern","COPY",FACE,{"derivedFrom":subQ1,"instanceName":"73"}),makeQuery(id+"F3.opPattern","COPY",FACE,{"derivedFrom":subQ1,"instanceName":"74"}),makeQuery(id+"F3.opPattern","COPY",FACE,{"derivedFrom":subQ1,"instanceName":"75"}),makeQuery(id+"F3.opPattern","COPY",FACE,{"derivedFrom":subQ1,"instanceName":"76"}),makeQuery(id+"F3.opPattern","COPY",FACE,{"derivedFrom":subQ1,"instanceName":"77"}),makeQuery(id+"F3.opPattern","COPY",FACE,{"derivedFrom":subQ1,"instanceName":"78"}),makeQuery(id+"F3.opPattern","COPY",FACE,{"derivedFrom":subQ1,"instanceName":"79"}),makeQuery(id+"F3.opPattern","COPY",FACE,{"derivedFrom":subQ1,"instanceName":"80"}),makeQuery(id+"F3.opPattern","COPY",FACE,{"derivedFrom":subQ1,"instanceName":"81"}),makeQuery(id+"F3.opPattern","COPY",FACE,{"derivedFrom":subQ1,"instanceName":"82"}),makeQuery(id+"F3.opPattern","COPY",FACE,{"derivedFrom":subQ1,"instanceName":"83"}),makeQuery(id+"F3.opPattern","COPY",FACE,{"derivedFrom":subQ1,"instanceName":"84"}),makeQuery(id+"F3.opPattern","COPY",FACE,{"derivedFrom":subQ1,"instanceName":"85"}),makeQuery(id+"F3.opPattern","COPY",FACE,{"derivedFrom":subQ1,"instanceName":"86"}),makeQuery(id+"F3.opPattern","COPY",FACE,{"derivedFrom":subQ1,"instanceName":"87"}),makeQuery(id+"F3.opPattern","COPY",FACE,{"derivedFrom":subQ1,"instanceName":"88"}),makeQuery(id+"F3.opPattern","COPY",FACE,{"derivedFrom":subQ1,"instanceName":"89"}),makeQuery(id+"F3.opPattern","COPY",FACE,{"derivedFrom":subQ1,"instanceName":"90"}),makeQuery(id+"F3.opPattern","COPY",FACE,{"derivedFrom":subQ1,"instanceName":"91"}),makeQuery(id+"F3.opPattern","COPY",FACE,{"derivedFrom":subQ1,"instanceName":"92"}),makeQuery(id+"F3.opPattern","COPY",FACE,{"derivedFrom":subQ1,"instanceName":"93"}),makeQuery(id+"F3.opPattern","COPY",FACE,{"derivedFrom":subQ1,"instanceName":"94"}),makeQuery(id+"F3.opPattern","COPY",FACE,{"derivedFrom":subQ1,"instanceName":"95"}),makeQuery(id+"F3.opPattern","COPY",FACE,{"derivedFrom":subQ1,"instanceName":"96"}),makeQuery(id+"F3.opPattern","COPY",FACE,{"derivedFrom":subQ1,"instanceName":"97"}),makeQuery(id+"F3.opPattern","COPY",FACE,{"derivedFrom":subQ1,"instanceName":"98"}),makeQuery(id+"F3.opPattern","COPY",FACE,{"derivedFrom":subQ1,"instanceName":"99"}),makeQuery(id+"F3.opPattern","COPY",FACE,{"derivedFrom":subQ1,"instanceName":"100"}),makeQuery(id+"F3.opPattern","COPY",FACE,{"derivedFrom":subQ1,"instanceName":"101"}),makeQuery(id+"F3.opPattern","COPY",FACE,{"derivedFrom":subQ1,"instanceName":"102"}),makeQuery(id+"F3.opPattern","COPY",FACE,{"derivedFrom":subQ1,"instanceName":"103"}),makeQuery(id+"F3.opPattern","COPY",FACE,{"derivedFrom":subQ1,"instanceName":"104"}),makeQuery(id+"F3.opPattern","COPY",FACE,{"derivedFrom":subQ1,"instanceName":"105"}),makeQuery(id+"F3.opPattern","COPY",FACE,{"derivedFrom":subQ1,"instanceName":"106"}),makeQuery(id+"F3.opPattern","COPY",FACE,{"derivedFrom":subQ1,"instanceName":"107"}),makeQuery(id+"F3.opPattern","COPY",FACE,{"derivedFrom":subQ1,"instanceName":"108"}),makeQuery(id+"F3.opPattern","COPY",FACE,{"derivedFrom":subQ1,"instanceName":"109"}),makeQuery(id+"F3.opPattern","COPY",FACE,{"derivedFrom":subQ1,"instanceName":"110"}),makeQuery(id+"F3.opPattern","COPY",FACE,{"derivedFrom":subQ1,"instanceName":"111"}),makeQuery(id+"F3.opPattern","COPY",FACE,{"derivedFrom":subQ1,"instanceName":"112"}),makeQuery(id+"F3.opPattern","COPY",FACE,{"derivedFrom":subQ1,"instanceName":"113"}),makeQuery(id+"F3.opPattern","COPY",FACE,{"derivedFrom":subQ1,"instanceName":"114"}),makeQuery(id+"F3.opPattern","COPY",FACE,{"derivedFrom":subQ1,"instanceName":"115"}),makeQuery(id+"F3.opPattern","COPY",FACE,{"derivedFrom":subQ1,"instanceName":"116"}),makeQuery(id+"F3.opPattern","COPY",FACE,{"derivedFrom":subQ1,"instanceName":"117"}),makeQuery(id+"F3.opPattern","COPY",FACE,{"derivedFrom":subQ1,"instanceName":"118"}),makeQuery(id+"F3.opPattern","COPY",FACE,{"derivedFrom":subQ1,"instanceName":"119"}),makeQuery(id+"F3.opPattern","COPY",FACE,{"derivedFrom":subQ1,"instanceName":"120"}),makeQuery(id+"F3.opPattern","COPY",FACE,{"derivedFrom":subQ1,"instanceName":"121"}),makeQuery(id+"F3.opPattern","COPY",FACE,{"derivedFrom":subQ1,"instanceName":"122"}),makeQuery(id+"F3.opPattern","COPY",FACE,{"derivedFrom":subQ1,"instanceName":"123"}),makeQuery(id+"F3.opPattern","COPY",FACE,{"derivedFrom":subQ1,"instanceName":"124"}),makeQuery(id+"F3.opPattern","COPY",FACE,{"derivedFrom":subQ1,"instanceName":"125"}),makeQuery(id+"F3.opPattern","COPY",FACE,{"derivedFrom":subQ1,"instanceName":"126"}),makeQuery(id+"F3.opPattern","COPY",FACE,{"derivedFrom":subQ1,"instanceName":"127"}),makeQuery(id+"F3.opPattern","COPY",FACE,{"derivedFrom":subQ1,"instanceName":"128"}),makeQuery(id+"F3.opPattern","COPY",FACE,{"derivedFrom":subQ1,"instanceName":"129"}),makeQuery(id+"F3.opPattern","COPY",FACE,{"derivedFrom":subQ1,"instanceName":"130"}),makeQuery(id+"F3.opPattern","COPY",FACE,{"derivedFrom":subQ1,"instanceName":"131"})]});}
            extrude(context, id + "F7", {"entities" : qUnion([Q0, Q1]), "endBound" : BoundingType.UP_TO_SURFACE, "oppositeDirection" : true, "endBoundEntityFace" : qUnion([Q2]), "depth" : 25.4 * mm});
        }
        {
            var Q0;
            Q0=makeQuery(id+"F7.opExtrude","SWEPT_EDGE",EDGE,{"disambiguationData":[OSD([sQuery(id+"F6.wireOp",EDGE,"E16"),sQuery(id+"F6.wireOp",EDGE,"E21.0")])]});
            var Q1;
            Q1=makeQuery(id+"F7.opExtrude","SWEPT_EDGE",EDGE,{"disambiguationData":[OSD([sQuery(id+"F6.wireOp",EDGE,"E17"),sQuery(id+"F6.wireOp",EDGE,"E21.0")])]});
            var Q2;
            Q2=makeQuery(id+"F7.opExtrude","SWEPT_EDGE",EDGE,{"disambiguationData":[OSD([sQuery(id+"F6.wireOp",EDGE,"E17"),sQuery(id+"F6.wireOp",EDGE,"E22.0")])]});
            var Q3;
            Q3=makeQuery(id+"F7.opExtrude","SWEPT_EDGE",EDGE,{"disambiguationData":[OSD([sQuery(id+"F6.wireOp",EDGE,"E16"),sQuery(id+"F6.wireOp",EDGE,"E22.0")])]});
            fillet(context, id + "F8", {"entities" : qUnion([Q0, Q1, Q2, Q3]), "radius" : 6.35 * mm, "tangentPropagation" : true, "allowEdgeOverflow" : false});
        }
        {
            var Q0;
            Q0=makeQuery(id+"F8.opFillet","BLEND_EDGE",EDGE,{"blendedFrom":[makeQuery(id+"F7.opExtrude","SWEPT_EDGE",EDGE,{"disambiguationData":[OSD([sQuery(id+"F6.wireOp",EDGE,"E17"),sQuery(id+"F6.wireOp",EDGE,"E22.0")])]}),makeQuery(id+"F7.opExtrude","SWEPT_FACE",FACE,{"disambiguationData":[OSD([sQuery(id+"F6.wireOp",EDGE,"E24")])]})],"blendedInto":[makeQuery(id+"F7.opExtrude","SWEPT_FACE",FACE,{"disambiguationData":[OSD([sQuery(id+"F6.wireOp",EDGE,"E24")])]})]});
            var Q1;
            Q1=makeQuery(id+"F8.opFillet","BLEND_EDGE",EDGE,{"blendedFrom":[makeQuery(id+"F7.opExtrude","SWEPT_EDGE",EDGE,{"disambiguationData":[OSD([sQuery(id+"F6.wireOp",EDGE,"E17"),sQuery(id+"F6.wireOp",EDGE,"E21.0")])]}),makeQuery(id+"F7.opExtrude","SWEPT_FACE",FACE,{"disambiguationData":[OSD([sQuery(id+"F6.wireOp",EDGE,"E24")])]})],"blendedInto":[makeQuery(id+"F7.opExtrude","SWEPT_FACE",FACE,{"disambiguationData":[OSD([sQuery(id+"F6.wireOp",EDGE,"E24")])]})]});
            fillet(context, id + "F9", {"entities" : qUnion([Q0, Q1]), "radius" : 3.17 * mm, "tangentPropagation" : true, "allowEdgeOverflow" : false});
        }
        {
            var Q0;
            Q0=makeQuery(id+"F7.opExtrude","SWEPT_BODY",BODY,{"disambiguationData":[OSD([sQuery(id+"F6.wireOp",EDGE,"E16"),sQuery(id+"F6.wireOp",EDGE,"E17"),sQuery(id+"F6.wireOp",EDGE,"E21.0"),sQuery(id+"F6.wireOp",EDGE,"E22.0")])]});
            var Q1;
            Q1=makeQuery(id+"F5.boolean.opBoolean","COPY",FACE,{"derivedFrom":makeQuery(id+"F5.opExtrude","SWEPT_FACE",FACE,{"disambiguationData":[OSD([sQuery(id+"F4.wireOp",EDGE,"E8")])]})});
            circularPattern(context, id + "F10", {"operationType" : NewBodyOperationType.REMOVE, "entities" : qUnion([Q0]), "axis" : qUnion([Q1]), "angle" : 360 * degree, "instanceCount" : 6, "equalSpace" : true});
        }
        {
            var Q0;
            {var subQ0=sQuery(id+"F0.wireOp",EDGE,"E7");var subQ1=makeQuery(id+"F2.opExtrude","CAP_FACE",FACE,{"disambiguationData":[OSD([sQuery(id+"F0.wireOp",EDGE,"E2"),sQuery(id+"F0.wireOp",EDGE,"E3"),sQuery(id+"F0.wireOp",EDGE,"E4"),sQuery(id+"F0.wireOp",EDGE,"E5"),sQuery(id+"F0.wireOp",EDGE,"E6"),subQ0])],"isStart":false});Q0=makeQuery(id+"F3.boolean.opBoolean","MERGE",FACE,{"derivedFrom":[makeQuery(id+"F1.opExtrude","CAP_FACE",FACE,{"disambiguationData":[OSD([sQuery(id+"F0.wireOp",EDGE,"E0"),sQuery(id+"F0.wireOp",EDGE,"E1"),subQ0])],"isStart":false}),subQ1,makeQuery(id+"F3.opPattern","COPY",FACE,{"derivedFrom":subQ1,"instanceName":"1"}),makeQuery(id+"F3.opPattern","COPY",FACE,{"derivedFrom":subQ1,"instanceName":"2"}),makeQuery(id+"F3.opPattern","COPY",FACE,{"derivedFrom":subQ1,"instanceName":"3"}),makeQuery(id+"F3.opPattern","COPY",FACE,{"derivedFrom":subQ1,"instanceName":"4"}),makeQuery(id+"F3.opPattern","COPY",FACE,{"derivedFrom":subQ1,"instanceName":"5"}),makeQuery(id+"F3.opPattern","COPY",FACE,{"derivedFrom":subQ1,"instanceName":"6"}),makeQuery(id+"F3.opPattern","COPY",FACE,{"derivedFrom":subQ1,"instanceName":"7"}),makeQuery(id+"F3.opPattern","COPY",FACE,{"derivedFrom":subQ1,"instanceName":"8"}),makeQuery(id+"F3.opPattern","COPY",FACE,{"derivedFrom":subQ1,"instanceName":"9"}),makeQuery(id+"F3.opPattern","COPY",FACE,{"derivedFrom":subQ1,"instanceName":"10"}),makeQuery(id+"F3.opPattern","COPY",FACE,{"derivedFrom":subQ1,"instanceName":"11"}),makeQuery(id+"F3.opPattern","COPY",FACE,{"derivedFrom":subQ1,"instanceName":"12"}),makeQuery(id+"F3.opPattern","COPY",FACE,{"derivedFrom":subQ1,"instanceName":"13"}),makeQuery(id+"F3.opPattern","COPY",FACE,{"derivedFrom":subQ1,"instanceName":"14"}),makeQuery(id+"F3.opPattern","COPY",FACE,{"derivedFrom":subQ1,"instanceName":"15"}),makeQuery(id+"F3.opPattern","COPY",FACE,{"derivedFrom":subQ1,"instanceName":"16"}),makeQuery(id+"F3.opPattern","COPY",FACE,{"derivedFrom":subQ1,"instanceName":"17"}),makeQuery(id+"F3.opPattern","COPY",FACE,{"derivedFrom":subQ1,"instanceName":"18"}),makeQuery(id+"F3.opPattern","COPY",FACE,{"derivedFrom":subQ1,"instanceName":"19"}),makeQuery(id+"F3.opPattern","COPY",FACE,{"derivedFrom":subQ1,"instanceName":"20"}),makeQuery(id+"F3.opPattern","COPY",FACE,{"derivedFrom":subQ1,"instanceName":"21"}),makeQuery(id+"F3.opPattern","COPY",FACE,{"derivedFrom":subQ1,"instanceName":"22"}),makeQuery(id+"F3.opPattern","COPY",FACE,{"derivedFrom":subQ1,"instanceName":"23"}),makeQuery(id+"F3.opPattern","COPY",FACE,{"derivedFrom":subQ1,"instanceName":"24"}),makeQuery(id+"F3.opPattern","COPY",FACE,{"derivedFrom":subQ1,"instanceName":"25"}),makeQuery(id+"F3.opPattern","COPY",FACE,{"derivedFrom":subQ1,"instanceName":"26"}),makeQuery(id+"F3.opPattern","COPY",FACE,{"derivedFrom":subQ1,"instanceName":"27"}),makeQuery(id+"F3.opPattern","COPY",FACE,{"derivedFrom":subQ1,"instanceName":"28"}),makeQuery(id+"F3.opPattern","COPY",FACE,{"derivedFrom":subQ1,"instanceName":"29"}),makeQuery(id+"F3.opPattern","COPY",FACE,{"derivedFrom":subQ1,"instanceName":"30"}),makeQuery(id+"F3.opPattern","COPY",FACE,{"derivedFrom":subQ1,"instanceName":"31"}),makeQuery(id+"F3.opPattern","COPY",FACE,{"derivedFrom":subQ1,"instanceName":"32"}),makeQuery(id+"F3.opPattern","COPY",FACE,{"derivedFrom":subQ1,"instanceName":"33"}),makeQuery(id+"F3.opPattern","COPY",FACE,{"derivedFrom":subQ1,"instanceName":"34"}),makeQuery(id+"F3.opPattern","COPY",FACE,{"derivedFrom":subQ1,"instanceName":"35"}),makeQuery(id+"F3.opPattern","COPY",FACE,{"derivedFrom":subQ1,"instanceName":"36"}),makeQuery(id+"F3.opPattern","COPY",FACE,{"derivedFrom":subQ1,"instanceName":"37"}),makeQuery(id+"F3.opPattern","COPY",FACE,{"derivedFrom":subQ1,"instanceName":"38"}),makeQuery(id+"F3.opPattern","COPY",FACE,{"derivedFrom":subQ1,"instanceName":"39"}),makeQuery(id+"F3.opPattern","COPY",FACE,{"derivedFrom":subQ1,"instanceName":"40"}),makeQuery(id+"F3.opPattern","COPY",FACE,{"derivedFrom":subQ1,"instanceName":"41"}),makeQuery(id+"F3.opPattern","COPY",FACE,{"derivedFrom":subQ1,"instanceName":"42"}),makeQuery(id+"F3.opPattern","COPY",FACE,{"derivedFrom":subQ1,"instanceName":"43"}),makeQuery(id+"F3.opPattern","COPY",FACE,{"derivedFrom":subQ1,"instanceName":"44"}),makeQuery(id+"F3.opPattern","COPY",FACE,{"derivedFrom":subQ1,"instanceName":"45"}),makeQuery(id+"F3.opPattern","COPY",FACE,{"derivedFrom":subQ1,"instanceName":"46"}),makeQuery(id+"F3.opPattern","COPY",FACE,{"derivedFrom":subQ1,"instanceName":"47"}),makeQuery(id+"F3.opPattern","COPY",FACE,{"derivedFrom":subQ1,"instanceName":"48"}),makeQuery(id+"F3.opPattern","COPY",FACE,{"derivedFrom":subQ1,"instanceName":"49"}),makeQuery(id+"F3.opPattern","COPY",FACE,{"derivedFrom":subQ1,"instanceName":"50"}),makeQuery(id+"F3.opPattern","COPY",FACE,{"derivedFrom":subQ1,"instanceName":"51"}),makeQuery(id+"F3.opPattern","COPY",FACE,{"derivedFrom":subQ1,"instanceName":"52"}),makeQuery(id+"F3.opPattern","COPY",FACE,{"derivedFrom":subQ1,"instanceName":"53"}),makeQuery(id+"F3.opPattern","COPY",FACE,{"derivedFrom":subQ1,"instanceName":"54"}),makeQuery(id+"F3.opPattern","COPY",FACE,{"derivedFrom":subQ1,"instanceName":"55"}),makeQuery(id+"F3.opPattern","COPY",FACE,{"derivedFrom":subQ1,"instanceName":"56"}),makeQuery(id+"F3.opPattern","COPY",FACE,{"derivedFrom":subQ1,"instanceName":"57"}),makeQuery(id+"F3.opPattern","COPY",FACE,{"derivedFrom":subQ1,"instanceName":"58"}),makeQuery(id+"F3.opPattern","COPY",FACE,{"derivedFrom":subQ1,"instanceName":"59"}),makeQuery(id+"F3.opPattern","COPY",FACE,{"derivedFrom":subQ1,"instanceName":"60"}),makeQuery(id+"F3.opPattern","COPY",FACE,{"derivedFrom":subQ1,"instanceName":"61"}),makeQuery(id+"F3.opPattern","COPY",FACE,{"derivedFrom":subQ1,"instanceName":"62"}),makeQuery(id+"F3.opPattern","COPY",FACE,{"derivedFrom":subQ1,"instanceName":"63"}),makeQuery(id+"F3.opPattern","COPY",FACE,{"derivedFrom":subQ1,"instanceName":"64"}),makeQuery(id+"F3.opPattern","COPY",FACE,{"derivedFrom":subQ1,"instanceName":"65"}),makeQuery(id+"F3.opPattern","COPY",FACE,{"derivedFrom":subQ1,"instanceName":"66"}),makeQuery(id+"F3.opPattern","COPY",FACE,{"derivedFrom":subQ1,"instanceName":"67"}),makeQuery(id+"F3.opPattern","COPY",FACE,{"derivedFrom":subQ1,"instanceName":"68"}),makeQuery(id+"F3.opPattern","COPY",FACE,{"derivedFrom":subQ1,"instanceName":"69"}),makeQuery(id+"F3.opPattern","COPY",FACE,{"derivedFrom":subQ1,"instanceName":"70"}),makeQuery(id+"F3.opPattern","COPY",FACE,{"derivedFrom":subQ1,"instanceName":"71"}),makeQuery(id+"F3.opPattern","COPY",FACE,{"derivedFrom":subQ1,"instanceName":"72"}),makeQuery(id+"F3.opPattern","COPY",FACE,{"derivedFrom":subQ1,"instanceName":"73"}),makeQuery(id+"F3.opPattern","COPY",FACE,{"derivedFrom":subQ1,"instanceName":"74"}),makeQuery(id+"F3.opPattern","COPY",FACE,{"derivedFrom":subQ1,"instanceName":"75"}),makeQuery(id+"F3.opPattern","COPY",FACE,{"derivedFrom":subQ1,"instanceName":"76"}),makeQuery(id+"F3.opPattern","COPY",FACE,{"derivedFrom":subQ1,"instanceName":"77"}),makeQuery(id+"F3.opPattern","COPY",FACE,{"derivedFrom":subQ1,"instanceName":"78"}),makeQuery(id+"F3.opPattern","COPY",FACE,{"derivedFrom":subQ1,"instanceName":"79"}),makeQuery(id+"F3.opPattern","COPY",FACE,{"derivedFrom":subQ1,"instanceName":"80"}),makeQuery(id+"F3.opPattern","COPY",FACE,{"derivedFrom":subQ1,"instanceName":"81"}),makeQuery(id+"F3.opPattern","COPY",FACE,{"derivedFrom":subQ1,"instanceName":"82"}),makeQuery(id+"F3.opPattern","COPY",FACE,{"derivedFrom":subQ1,"instanceName":"83"}),makeQuery(id+"F3.opPattern","COPY",FACE,{"derivedFrom":subQ1,"instanceName":"84"}),makeQuery(id+"F3.opPattern","COPY",FACE,{"derivedFrom":subQ1,"instanceName":"85"}),makeQuery(id+"F3.opPattern","COPY",FACE,{"derivedFrom":subQ1,"instanceName":"86"}),makeQuery(id+"F3.opPattern","COPY",FACE,{"derivedFrom":subQ1,"instanceName":"87"}),makeQuery(id+"F3.opPattern","COPY",FACE,{"derivedFrom":subQ1,"instanceName":"88"}),makeQuery(id+"F3.opPattern","COPY",FACE,{"derivedFrom":subQ1,"instanceName":"89"}),makeQuery(id+"F3.opPattern","COPY",FACE,{"derivedFrom":subQ1,"instanceName":"90"}),makeQuery(id+"F3.opPattern","COPY",FACE,{"derivedFrom":subQ1,"instanceName":"91"}),makeQuery(id+"F3.opPattern","COPY",FACE,{"derivedFrom":subQ1,"instanceName":"92"}),makeQuery(id+"F3.opPattern","COPY",FACE,{"derivedFrom":subQ1,"instanceName":"93"}),makeQuery(id+"F3.opPattern","COPY",FACE,{"derivedFrom":subQ1,"instanceName":"94"}),makeQuery(id+"F3.opPattern","COPY",FACE,{"derivedFrom":subQ1,"instanceName":"95"}),makeQuery(id+"F3.opPattern","COPY",FACE,{"derivedFrom":subQ1,"instanceName":"96"}),makeQuery(id+"F3.opPattern","COPY",FACE,{"derivedFrom":subQ1,"instanceName":"97"}),makeQuery(id+"F3.opPattern","COPY",FACE,{"derivedFrom":subQ1,"instanceName":"98"}),makeQuery(id+"F3.opPattern","COPY",FACE,{"derivedFrom":subQ1,"instanceName":"99"}),makeQuery(id+"F3.opPattern","COPY",FACE,{"derivedFrom":subQ1,"instanceName":"100"}),makeQuery(id+"F3.opPattern","COPY",FACE,{"derivedFrom":subQ1,"instanceName":"101"}),makeQuery(id+"F3.opPattern","COPY",FACE,{"derivedFrom":subQ1,"instanceName":"102"}),makeQuery(id+"F3.opPattern","COPY",FACE,{"derivedFrom":subQ1,"instanceName":"103"}),makeQuery(id+"F3.opPattern","COPY",FACE,{"derivedFrom":subQ1,"instanceName":"104"}),makeQuery(id+"F3.opPattern","COPY",FACE,{"derivedFrom":subQ1,"instanceName":"105"}),makeQuery(id+"F3.opPattern","COPY",FACE,{"derivedFrom":subQ1,"instanceName":"106"}),makeQuery(id+"F3.opPattern","COPY",FACE,{"derivedFrom":subQ1,"instanceName":"107"}),makeQuery(id+"F3.opPattern","COPY",FACE,{"derivedFrom":subQ1,"instanceName":"108"}),makeQuery(id+"F3.opPattern","COPY",FACE,{"derivedFrom":subQ1,"instanceName":"109"}),makeQuery(id+"F3.opPattern","COPY",FACE,{"derivedFrom":subQ1,"instanceName":"110"}),makeQuery(id+"F3.opPattern","COPY",FACE,{"derivedFrom":subQ1,"instanceName":"111"}),makeQuery(id+"F3.opPattern","COPY",FACE,{"derivedFrom":subQ1,"instanceName":"112"}),makeQuery(id+"F3.opPattern","COPY",FACE,{"derivedFrom":subQ1,"instanceName":"113"}),makeQuery(id+"F3.opPattern","COPY",FACE,{"derivedFrom":subQ1,"instanceName":"114"}),makeQuery(id+"F3.opPattern","COPY",FACE,{"derivedFrom":subQ1,"instanceName":"115"}),makeQuery(id+"F3.opPattern","COPY",FACE,{"derivedFrom":subQ1,"instanceName":"116"}),makeQuery(id+"F3.opPattern","COPY",FACE,{"derivedFrom":subQ1,"instanceName":"117"}),makeQuery(id+"F3.opPattern","COPY",FACE,{"derivedFrom":subQ1,"instanceName":"118"}),makeQuery(id+"F3.opPattern","COPY",FACE,{"derivedFrom":subQ1,"instanceName":"119"}),makeQuery(id+"F3.opPattern","COPY",FACE,{"derivedFrom":subQ1,"instanceName":"120"}),makeQuery(id+"F3.opPattern","COPY",FACE,{"derivedFrom":subQ1,"instanceName":"121"}),makeQuery(id+"F3.opPattern","COPY",FACE,{"derivedFrom":subQ1,"instanceName":"122"}),makeQuery(id+"F3.opPattern","COPY",FACE,{"derivedFrom":subQ1,"instanceName":"123"}),makeQuery(id+"F3.opPattern","COPY",FACE,{"derivedFrom":subQ1,"instanceName":"124"}),makeQuery(id+"F3.opPattern","COPY",FACE,{"derivedFrom":subQ1,"instanceName":"125"}),makeQuery(id+"F3.opPattern","COPY",FACE,{"derivedFrom":subQ1,"instanceName":"126"}),makeQuery(id+"F3.opPattern","COPY",FACE,{"derivedFrom":subQ1,"instanceName":"127"}),makeQuery(id+"F3.opPattern","COPY",FACE,{"derivedFrom":subQ1,"instanceName":"128"}),makeQuery(id+"F3.opPattern","COPY",FACE,{"derivedFrom":subQ1,"instanceName":"129"}),makeQuery(id+"F3.opPattern","COPY",FACE,{"derivedFrom":subQ1,"instanceName":"130"}),makeQuery(id+"F3.opPattern","COPY",FACE,{"derivedFrom":subQ1,"instanceName":"131"})]});}
            var sketch = newSketch(context, id + "F11", { "sketchPlane" : qUnion([Q0])});
            skCircle(sketch, "E27.0", {"center": v(0, 0) * mm, "radius": 14.29 * mm});
            skCircle(sketch, "E27.1", {"center": v(23.81, 0) * mm, "radius": 2.41 * mm});
            skCircle(sketch, "E27.2", {"center": v(11.9, 20.62) * mm, "radius": 2.41 * mm});
            skCircle(sketch, "E27.5", {"center": v(-11.9, -20.62) * mm, "radius": 2.41 * mm});
            skCircle(sketch, "E28.0", {"center": v(-23.81, 0) * mm, "radius": 2.41 * mm});
            skCircle(sketch, "E28.1", {"center": v(11.9, -20.62) * mm, "radius": 2.41 * mm});
            skCircle(sketch, "E28.2", {"center": v(-11.9, 20.62) * mm, "radius": 2.41 * mm});
            skArc(sketch, "E29.0", {"start": v(27.6, -9.98) * mm, "mid": v(23.37, -13.5) * mm, "end": v(22.44, -18.9) * mm});
            skArc(sketch, "E29.1", {"start": v(29.08, -8.9) * mm, "mid": v(28.42, -9.55) * mm, "end": v(27.6, -9.98) * mm});
            skArc(sketch, "E29.2", {"start": v(22.44, -18.9) * mm, "mid": v(22.48, -19.84) * mm, "end": v(22.24, -20.74) * mm});
            skArc(sketch, "E29.3", {"start": v(6.84, -29.63) * mm, "mid": v(5.94, -29.38) * mm, "end": v(5.15, -28.89) * mm});
            skArc(sketch, "E29.4", {"start": v(5.15, -28.89) * mm, "mid": v(0, -26.99) * mm, "end": v(-5.15, -28.89) * mm});
            skArc(sketch, "E29.5", {"start": v(-5.15, -28.89) * mm, "mid": v(-5.94, -29.38) * mm, "end": v(-6.84, -29.63) * mm});
            skArc(sketch, "E29.6", {"start": v(27.6, 9.98) * mm, "mid": v(28.42, 9.55) * mm, "end": v(29.08, 8.9) * mm});
            skArc(sketch, "E29.7", {"start": v(22.44, 18.9) * mm, "mid": v(23.37, 13.5) * mm, "end": v(27.6, 9.98) * mm});
            skArc(sketch, "E29.8", {"start": v(22.24, 20.74) * mm, "mid": v(22.48, 19.84) * mm, "end": v(22.44, 18.9) * mm});
            skArc(sketch, "E29.9", {"start": v(5.15, 28.89) * mm, "mid": v(5.94, 29.38) * mm, "end": v(6.84, 29.63) * mm});
            skArc(sketch, "E29.10", {"start": v(-5.15, 28.89) * mm, "mid": v(0, 26.99) * mm, "end": v(5.15, 28.89) * mm});
            skArc(sketch, "E29.11", {"start": v(-6.84, 29.63) * mm, "mid": v(-5.94, 29.38) * mm, "end": v(-5.15, 28.89) * mm});
            skArc(sketch, "E29.12", {"start": v(-22.44, 18.9) * mm, "mid": v(-22.48, 19.84) * mm, "end": v(-22.24, 20.74) * mm});
            skArc(sketch, "E29.13", {"start": v(-27.6, 9.98) * mm, "mid": v(-23.37, 13.5) * mm, "end": v(-22.44, 18.9) * mm});
            skArc(sketch, "E29.14", {"start": v(-29.08, 8.9) * mm, "mid": v(-28.42, 9.55) * mm, "end": v(-27.6, 9.98) * mm});
            skArc(sketch, "E29.15", {"start": v(-27.6, -9.98) * mm, "mid": v(-28.42, -9.55) * mm, "end": v(-29.08, -8.9) * mm});
            skArc(sketch, "E29.16", {"start": v(-22.44, -18.9) * mm, "mid": v(-23.37, -13.5) * mm, "end": v(-27.6, -9.98) * mm});
            skArc(sketch, "E29.17", {"start": v(-22.24, -20.74) * mm, "mid": v(-22.48, -19.84) * mm, "end": v(-22.44, -18.9) * mm});
            skArc(sketch, "E30", {"start": v(29.08, -8.9) * mm, "mid": v(30.4, 0) * mm, "end": v(29.08, 8.9) * mm});
            skArc(sketch, "E31.trimOffspring", {"start": v(22.24, 20.74) * mm, "mid": v(15.2, 26.33) * mm, "end": v(6.84, 29.63) * mm});
            skArc(sketch, "E32.trimOffspring", {"start": v(-6.84, 29.63) * mm, "mid": v(-15.2, 26.33) * mm, "end": v(-22.24, 20.74) * mm});
            skArc(sketch, "E33.trimOffspring", {"start": v(-29.08, 8.9) * mm, "mid": v(-30.4, 0) * mm, "end": v(-29.08, -8.9) * mm});
            skArc(sketch, "E34.trimOffspring", {"start": v(-22.24, -20.74) * mm, "mid": v(-15.2, -26.33) * mm, "end": v(-6.84, -29.63) * mm});
            skArc(sketch, "E35.trimOffspring", {"start": v(6.84, -29.63) * mm, "mid": v(15.2, -26.33) * mm, "end": v(22.24, -20.74) * mm});
            skSolve(sketch);
        }
        {
            var Q0;
            Q0=qSketchRegion(id+"F11",true);
            extrude(context, id + "F12", {"entities" : qUnion([Q0]), "depth" : 3.17 * mm});
        }
        {
            var Q0;
            {var subQ0=sQuery(id+"F0.wireOp",EDGE,"E7");var subQ1=makeQuery(id+"F2.opExtrude","CAP_FACE",FACE,{"disambiguationData":[OSD([sQuery(id+"F0.wireOp",EDGE,"E2"),sQuery(id+"F0.wireOp",EDGE,"E3"),sQuery(id+"F0.wireOp",EDGE,"E4"),sQuery(id+"F0.wireOp",EDGE,"E5"),sQuery(id+"F0.wireOp",EDGE,"E6"),subQ0])],"isStart":true});Q0=makeQuery(id+"F3.boolean.opBoolean","MERGE",FACE,{"derivedFrom":[makeQuery(id+"F1.opExtrude","CAP_FACE",FACE,{"disambiguationData":[OSD([sQuery(id+"F0.wireOp",EDGE,"E0"),sQuery(id+"F0.wireOp",EDGE,"E1"),subQ0])],"isStart":true}),subQ1,makeQuery(id+"F3.opPattern","COPY",FACE,{"derivedFrom":subQ1,"instanceName":"1"}),makeQuery(id+"F3.opPattern","COPY",FACE,{"derivedFrom":subQ1,"instanceName":"2"}),makeQuery(id+"F3.opPattern","COPY",FACE,{"derivedFrom":subQ1,"instanceName":"3"}),makeQuery(id+"F3.opPattern","COPY",FACE,{"derivedFrom":subQ1,"instanceName":"4"}),makeQuery(id+"F3.opPattern","COPY",FACE,{"derivedFrom":subQ1,"instanceName":"5"}),makeQuery(id+"F3.opPattern","COPY",FACE,{"derivedFrom":subQ1,"instanceName":"6"}),makeQuery(id+"F3.opPattern","COPY",FACE,{"derivedFrom":subQ1,"instanceName":"7"}),makeQuery(id+"F3.opPattern","COPY",FACE,{"derivedFrom":subQ1,"instanceName":"8"}),makeQuery(id+"F3.opPattern","COPY",FACE,{"derivedFrom":subQ1,"instanceName":"9"}),makeQuery(id+"F3.opPattern","COPY",FACE,{"derivedFrom":subQ1,"instanceName":"10"}),makeQuery(id+"F3.opPattern","COPY",FACE,{"derivedFrom":subQ1,"instanceName":"11"}),makeQuery(id+"F3.opPattern","COPY",FACE,{"derivedFrom":subQ1,"instanceName":"12"}),makeQuery(id+"F3.opPattern","COPY",FACE,{"derivedFrom":subQ1,"instanceName":"13"}),makeQuery(id+"F3.opPattern","COPY",FACE,{"derivedFrom":subQ1,"instanceName":"14"}),makeQuery(id+"F3.opPattern","COPY",FACE,{"derivedFrom":subQ1,"instanceName":"15"}),makeQuery(id+"F3.opPattern","COPY",FACE,{"derivedFrom":subQ1,"instanceName":"16"}),makeQuery(id+"F3.opPattern","COPY",FACE,{"derivedFrom":subQ1,"instanceName":"17"}),makeQuery(id+"F3.opPattern","COPY",FACE,{"derivedFrom":subQ1,"instanceName":"18"}),makeQuery(id+"F3.opPattern","COPY",FACE,{"derivedFrom":subQ1,"instanceName":"19"}),makeQuery(id+"F3.opPattern","COPY",FACE,{"derivedFrom":subQ1,"instanceName":"20"}),makeQuery(id+"F3.opPattern","COPY",FACE,{"derivedFrom":subQ1,"instanceName":"21"}),makeQuery(id+"F3.opPattern","COPY",FACE,{"derivedFrom":subQ1,"instanceName":"22"}),makeQuery(id+"F3.opPattern","COPY",FACE,{"derivedFrom":subQ1,"instanceName":"23"}),makeQuery(id+"F3.opPattern","COPY",FACE,{"derivedFrom":subQ1,"instanceName":"24"}),makeQuery(id+"F3.opPattern","COPY",FACE,{"derivedFrom":subQ1,"instanceName":"25"}),makeQuery(id+"F3.opPattern","COPY",FACE,{"derivedFrom":subQ1,"instanceName":"26"}),makeQuery(id+"F3.opPattern","COPY",FACE,{"derivedFrom":subQ1,"instanceName":"27"}),makeQuery(id+"F3.opPattern","COPY",FACE,{"derivedFrom":subQ1,"instanceName":"28"}),makeQuery(id+"F3.opPattern","COPY",FACE,{"derivedFrom":subQ1,"instanceName":"29"}),makeQuery(id+"F3.opPattern","COPY",FACE,{"derivedFrom":subQ1,"instanceName":"30"}),makeQuery(id+"F3.opPattern","COPY",FACE,{"derivedFrom":subQ1,"instanceName":"31"}),makeQuery(id+"F3.opPattern","COPY",FACE,{"derivedFrom":subQ1,"instanceName":"32"}),makeQuery(id+"F3.opPattern","COPY",FACE,{"derivedFrom":subQ1,"instanceName":"33"}),makeQuery(id+"F3.opPattern","COPY",FACE,{"derivedFrom":subQ1,"instanceName":"34"}),makeQuery(id+"F3.opPattern","COPY",FACE,{"derivedFrom":subQ1,"instanceName":"35"}),makeQuery(id+"F3.opPattern","COPY",FACE,{"derivedFrom":subQ1,"instanceName":"36"}),makeQuery(id+"F3.opPattern","COPY",FACE,{"derivedFrom":subQ1,"instanceName":"37"}),makeQuery(id+"F3.opPattern","COPY",FACE,{"derivedFrom":subQ1,"instanceName":"38"}),makeQuery(id+"F3.opPattern","COPY",FACE,{"derivedFrom":subQ1,"instanceName":"39"}),makeQuery(id+"F3.opPattern","COPY",FACE,{"derivedFrom":subQ1,"instanceName":"40"}),makeQuery(id+"F3.opPattern","COPY",FACE,{"derivedFrom":subQ1,"instanceName":"41"}),makeQuery(id+"F3.opPattern","COPY",FACE,{"derivedFrom":subQ1,"instanceName":"42"}),makeQuery(id+"F3.opPattern","COPY",FACE,{"derivedFrom":subQ1,"instanceName":"43"}),makeQuery(id+"F3.opPattern","COPY",FACE,{"derivedFrom":subQ1,"instanceName":"44"}),makeQuery(id+"F3.opPattern","COPY",FACE,{"derivedFrom":subQ1,"instanceName":"45"}),makeQuery(id+"F3.opPattern","COPY",FACE,{"derivedFrom":subQ1,"instanceName":"46"}),makeQuery(id+"F3.opPattern","COPY",FACE,{"derivedFrom":subQ1,"instanceName":"47"}),makeQuery(id+"F3.opPattern","COPY",FACE,{"derivedFrom":subQ1,"instanceName":"48"}),makeQuery(id+"F3.opPattern","COPY",FACE,{"derivedFrom":subQ1,"instanceName":"49"}),makeQuery(id+"F3.opPattern","COPY",FACE,{"derivedFrom":subQ1,"instanceName":"50"}),makeQuery(id+"F3.opPattern","COPY",FACE,{"derivedFrom":subQ1,"instanceName":"51"}),makeQuery(id+"F3.opPattern","COPY",FACE,{"derivedFrom":subQ1,"instanceName":"52"}),makeQuery(id+"F3.opPattern","COPY",FACE,{"derivedFrom":subQ1,"instanceName":"53"}),makeQuery(id+"F3.opPattern","COPY",FACE,{"derivedFrom":subQ1,"instanceName":"54"}),makeQuery(id+"F3.opPattern","COPY",FACE,{"derivedFrom":subQ1,"instanceName":"55"}),makeQuery(id+"F3.opPattern","COPY",FACE,{"derivedFrom":subQ1,"instanceName":"56"}),makeQuery(id+"F3.opPattern","COPY",FACE,{"derivedFrom":subQ1,"instanceName":"57"}),makeQuery(id+"F3.opPattern","COPY",FACE,{"derivedFrom":subQ1,"instanceName":"58"}),makeQuery(id+"F3.opPattern","COPY",FACE,{"derivedFrom":subQ1,"instanceName":"59"}),makeQuery(id+"F3.opPattern","COPY",FACE,{"derivedFrom":subQ1,"instanceName":"60"}),makeQuery(id+"F3.opPattern","COPY",FACE,{"derivedFrom":subQ1,"instanceName":"61"}),makeQuery(id+"F3.opPattern","COPY",FACE,{"derivedFrom":subQ1,"instanceName":"62"}),makeQuery(id+"F3.opPattern","COPY",FACE,{"derivedFrom":subQ1,"instanceName":"63"}),makeQuery(id+"F3.opPattern","COPY",FACE,{"derivedFrom":subQ1,"instanceName":"64"}),makeQuery(id+"F3.opPattern","COPY",FACE,{"derivedFrom":subQ1,"instanceName":"65"}),makeQuery(id+"F3.opPattern","COPY",FACE,{"derivedFrom":subQ1,"instanceName":"66"}),makeQuery(id+"F3.opPattern","COPY",FACE,{"derivedFrom":subQ1,"instanceName":"67"}),makeQuery(id+"F3.opPattern","COPY",FACE,{"derivedFrom":subQ1,"instanceName":"68"}),makeQuery(id+"F3.opPattern","COPY",FACE,{"derivedFrom":subQ1,"instanceName":"69"}),makeQuery(id+"F3.opPattern","COPY",FACE,{"derivedFrom":subQ1,"instanceName":"70"}),makeQuery(id+"F3.opPattern","COPY",FACE,{"derivedFrom":subQ1,"instanceName":"71"}),makeQuery(id+"F3.opPattern","COPY",FACE,{"derivedFrom":subQ1,"instanceName":"72"}),makeQuery(id+"F3.opPattern","COPY",FACE,{"derivedFrom":subQ1,"instanceName":"73"}),makeQuery(id+"F3.opPattern","COPY",FACE,{"derivedFrom":subQ1,"instanceName":"74"}),makeQuery(id+"F3.opPattern","COPY",FACE,{"derivedFrom":subQ1,"instanceName":"75"}),makeQuery(id+"F3.opPattern","COPY",FACE,{"derivedFrom":subQ1,"instanceName":"76"}),makeQuery(id+"F3.opPattern","COPY",FACE,{"derivedFrom":subQ1,"instanceName":"77"}),makeQuery(id+"F3.opPattern","COPY",FACE,{"derivedFrom":subQ1,"instanceName":"78"}),makeQuery(id+"F3.opPattern","COPY",FACE,{"derivedFrom":subQ1,"instanceName":"79"}),makeQuery(id+"F3.opPattern","COPY",FACE,{"derivedFrom":subQ1,"instanceName":"80"}),makeQuery(id+"F3.opPattern","COPY",FACE,{"derivedFrom":subQ1,"instanceName":"81"}),makeQuery(id+"F3.opPattern","COPY",FACE,{"derivedFrom":subQ1,"instanceName":"82"}),makeQuery(id+"F3.opPattern","COPY",FACE,{"derivedFrom":subQ1,"instanceName":"83"}),makeQuery(id+"F3.opPattern","COPY",FACE,{"derivedFrom":subQ1,"instanceName":"84"}),makeQuery(id+"F3.opPattern","COPY",FACE,{"derivedFrom":subQ1,"instanceName":"85"}),makeQuery(id+"F3.opPattern","COPY",FACE,{"derivedFrom":subQ1,"instanceName":"86"}),makeQuery(id+"F3.opPattern","COPY",FACE,{"derivedFrom":subQ1,"instanceName":"87"}),makeQuery(id+"F3.opPattern","COPY",FACE,{"derivedFrom":subQ1,"instanceName":"88"}),makeQuery(id+"F3.opPattern","COPY",FACE,{"derivedFrom":subQ1,"instanceName":"89"}),makeQuery(id+"F3.opPattern","COPY",FACE,{"derivedFrom":subQ1,"instanceName":"90"}),makeQuery(id+"F3.opPattern","COPY",FACE,{"derivedFrom":subQ1,"instanceName":"91"}),makeQuery(id+"F3.opPattern","COPY",FACE,{"derivedFrom":subQ1,"instanceName":"92"}),makeQuery(id+"F3.opPattern","COPY",FACE,{"derivedFrom":subQ1,"instanceName":"93"}),makeQuery(id+"F3.opPattern","COPY",FACE,{"derivedFrom":subQ1,"instanceName":"94"}),makeQuery(id+"F3.opPattern","COPY",FACE,{"derivedFrom":subQ1,"instanceName":"95"}),makeQuery(id+"F3.opPattern","COPY",FACE,{"derivedFrom":subQ1,"instanceName":"96"}),makeQuery(id+"F3.opPattern","COPY",FACE,{"derivedFrom":subQ1,"instanceName":"97"}),makeQuery(id+"F3.opPattern","COPY",FACE,{"derivedFrom":subQ1,"instanceName":"98"}),makeQuery(id+"F3.opPattern","COPY",FACE,{"derivedFrom":subQ1,"instanceName":"99"}),makeQuery(id+"F3.opPattern","COPY",FACE,{"derivedFrom":subQ1,"instanceName":"100"}),makeQuery(id+"F3.opPattern","COPY",FACE,{"derivedFrom":subQ1,"instanceName":"101"}),makeQuery(id+"F3.opPattern","COPY",FACE,{"derivedFrom":subQ1,"instanceName":"102"}),makeQuery(id+"F3.opPattern","COPY",FACE,{"derivedFrom":subQ1,"instanceName":"103"}),makeQuery(id+"F3.opPattern","COPY",FACE,{"derivedFrom":subQ1,"instanceName":"104"}),makeQuery(id+"F3.opPattern","COPY",FACE,{"derivedFrom":subQ1,"instanceName":"105"}),makeQuery(id+"F3.opPattern","COPY",FACE,{"derivedFrom":subQ1,"instanceName":"106"}),makeQuery(id+"F3.opPattern","COPY",FACE,{"derivedFrom":subQ1,"instanceName":"107"}),makeQuery(id+"F3.opPattern","COPY",FACE,{"derivedFrom":subQ1,"instanceName":"108"}),makeQuery(id+"F3.opPattern","COPY",FACE,{"derivedFrom":subQ1,"instanceName":"109"}),makeQuery(id+"F3.opPattern","COPY",FACE,{"derivedFrom":subQ1,"instanceName":"110"}),makeQuery(id+"F3.opPattern","COPY",FACE,{"derivedFrom":subQ1,"instanceName":"111"}),makeQuery(id+"F3.opPattern","COPY",FACE,{"derivedFrom":subQ1,"instanceName":"112"}),makeQuery(id+"F3.opPattern","COPY",FACE,{"derivedFrom":subQ1,"instanceName":"113"}),makeQuery(id+"F3.opPattern","COPY",FACE,{"derivedFrom":subQ1,"instanceName":"114"}),makeQuery(id+"F3.opPattern","COPY",FACE,{"derivedFrom":subQ1,"instanceName":"115"}),makeQuery(id+"F3.opPattern","COPY",FACE,{"derivedFrom":subQ1,"instanceName":"116"}),makeQuery(id+"F3.opPattern","COPY",FACE,{"derivedFrom":subQ1,"instanceName":"117"}),makeQuery(id+"F3.opPattern","COPY",FACE,{"derivedFrom":subQ1,"instanceName":"118"}),makeQuery(id+"F3.opPattern","COPY",FACE,{"derivedFrom":subQ1,"instanceName":"119"}),makeQuery(id+"F3.opPattern","COPY",FACE,{"derivedFrom":subQ1,"instanceName":"120"}),makeQuery(id+"F3.opPattern","COPY",FACE,{"derivedFrom":subQ1,"instanceName":"121"}),makeQuery(id+"F3.opPattern","COPY",FACE,{"derivedFrom":subQ1,"instanceName":"122"}),makeQuery(id+"F3.opPattern","COPY",FACE,{"derivedFrom":subQ1,"instanceName":"123"}),makeQuery(id+"F3.opPattern","COPY",FACE,{"derivedFrom":subQ1,"instanceName":"124"}),makeQuery(id+"F3.opPattern","COPY",FACE,{"derivedFrom":subQ1,"instanceName":"125"}),makeQuery(id+"F3.opPattern","COPY",FACE,{"derivedFrom":subQ1,"instanceName":"126"}),makeQuery(id+"F3.opPattern","COPY",FACE,{"derivedFrom":subQ1,"instanceName":"127"}),makeQuery(id+"F3.opPattern","COPY",FACE,{"derivedFrom":subQ1,"instanceName":"128"}),makeQuery(id+"F3.opPattern","COPY",FACE,{"derivedFrom":subQ1,"instanceName":"129"}),makeQuery(id+"F3.opPattern","COPY",FACE,{"derivedFrom":subQ1,"instanceName":"130"}),makeQuery(id+"F3.opPattern","COPY",FACE,{"derivedFrom":subQ1,"instanceName":"131"})]});}
            var sketch = newSketch(context, id + "F13", { "sketchPlane" : qUnion([Q0])});
            skCircle(sketch, "E36.0", {"center": v(-23.81, 0) * mm, "radius": 2.41 * mm});
            skCircle(sketch, "E36.1", {"center": v(-11.9, 20.62) * mm, "radius": 2.41 * mm});
            skCircle(sketch, "E36.2", {"center": v(11.9, 20.62) * mm, "radius": 2.41 * mm});
            skCircle(sketch, "E36.3", {"center": v(23.81, 0) * mm, "radius": 2.41 * mm});
            skCircle(sketch, "E36.4", {"center": v(11.9, -20.62) * mm, "radius": 2.41 * mm});
            skCircle(sketch, "E36.5", {"center": v(-11.9, -20.62) * mm, "radius": 2.41 * mm});
            skSolve(sketch);
        }
        {
            var Q0;
            Q0=sQuery(id+"F13.wireOp",VERTEX,"E36.4.center");
            var Q1;
            Q1=sQuery(id+"F13.wireOp",VERTEX,"E36.3.center");
            var Q2;
            Q2=sQuery(id+"F13.wireOp",VERTEX,"E36.2.center");
            var Q3;
            Q3=sQuery(id+"F13.wireOp",VERTEX,"E36.1.center");
            var Q4;
            Q4=sQuery(id+"F13.wireOp",VERTEX,"E36.0.center");
            var Q5;
            Q5=sQuery(id+"F13.wireOp",VERTEX,"E36.5.center");
            var Q6;
            Q6=makeQuery(id+"F1.opExtrude","SWEPT_BODY",BODY,{"disambiguationData":[OSD([sQuery(id+"F0.wireOp",EDGE,"E0"),sQuery(id+"F0.wireOp",EDGE,"E1"),sQuery(id+"F0.wireOp",EDGE,"E7")])]});
            hole(context, id + "F14", {"style" : HoleStyle.C_BORE, "holeDiameter" : 4.83 * mm, "cBoreDiameter" : 7.94 * mm, "cBoreDepth" : 4.83 * mm, "endStyle" : HoleEndStyle.THROUGH, "locations" : qUnion([Q0, Q1, Q2, Q3, Q4, Q5]), "scope" : qUnion([Q6])});
        }
    });
